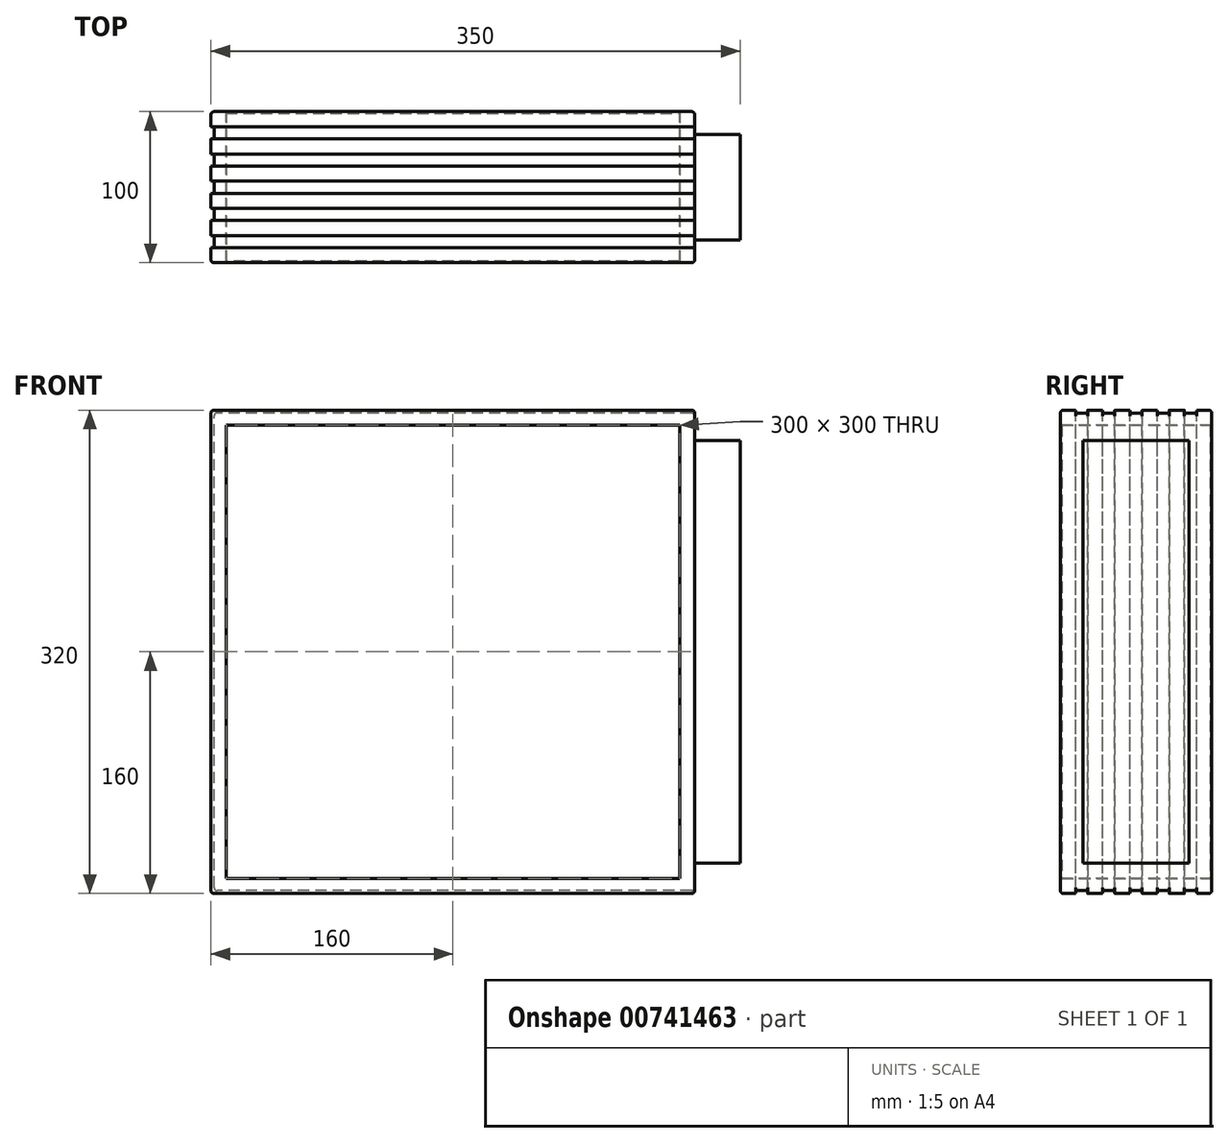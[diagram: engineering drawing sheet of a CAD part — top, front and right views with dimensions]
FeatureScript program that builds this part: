
annotation { "Feature Type Name" : "Feature", "Feature Type Description" : "" }
export const myFeature = defineFeature(function(context is Context, id is Id, definition is map)
    precondition{}
    {
        {
            var Q0;
            Q0=qCreatedBy(makeId("Front.planeOp"),FACE);
            var sketch = newSketch(context, id + "F0", { "sketchPlane" : qUnion([Q0])});
            skLineSegment(sketch, "E0.bottom", {"start": v(-1550, 0) * mm, "end": v(-1500, 0) * mm});
            skLineSegment(sketch, "E0.top", {"start": v(-1550, -2720) * mm, "end": v(-1500, -2720) * mm});
            skLineSegment(sketch, "E0.left", {"start": v(-1550, 0) * mm, "end": v(-1550, -2720) * mm});
            skLineSegment(sketch, "E0.right", {"start": v(-1500, 0) * mm, "end": v(-1500, -2720) * mm});
            skLineSegment(sketch, "E1.MirrorCS", {"start": v(1550, -2720) * mm, "end": v(1500, -2720) * mm});
            skLineSegment(sketch, "E2.MirrorCS", {"start": v(1500, 0) * mm, "end": v(1500, -2720) * mm});
            skLineSegment(sketch, "E3.MirrorCS", {"start": v(1550, 0) * mm, "end": v(1500, 0) * mm});
            skLineSegment(sketch, "E4.MirrorCS", {"start": v(1550, 0) * mm, "end": v(1550, -2720) * mm});
            skSolve(sketch);
        }
        {
            var Q0;
            Q0=qSketchRegion(id+"F0",true);
            extrude(context, id + "F1", {"entities" : qUnion([Q0]), "depth" : 100 * mm, "offsetDistance" : 25 * mm});
        }
        {
            var Q0;
            Q0=makeQuery(id+"F1.opExtrude","SWEPT_FACE",FACE,{"disambiguationData":[OSD([sQuery(id+"F0.wireOp",EDGE,"E0.bottom")])]});
            var sketch = newSketch(context, id + "F2", { "sketchPlane" : qUnion([Q0])});
            skLineSegment(sketch, "E5.bottom", {"start": v(-1550, -100) * mm, "end": v(-1870, -100) * mm});
            skLineSegment(sketch, "E5.top", {"start": v(-1550, 0) * mm, "end": v(-1870, 0) * mm});
            skLineSegment(sketch, "E5.left", {"start": v(-1550, -100) * mm, "end": v(-1550, 0) * mm});
            skLineSegment(sketch, "E5.right", {"start": v(-1870, -100) * mm, "end": v(-1870, 0) * mm});
            skLineSegment(sketch, "E6.bottom", {"start": v(-1500, -100) * mm, "end": v(1500, -100) * mm});
            skLineSegment(sketch, "E6.top", {"start": v(-1500, 0) * mm, "end": v(1500, 0) * mm});
            skLineSegment(sketch, "E6.left", {"start": v(-1500, -100) * mm, "end": v(-1500, 0) * mm});
            skLineSegment(sketch, "E6.right", {"start": v(1500, -100) * mm, "end": v(1500, 0) * mm});
            skLineSegment(sketch, "E7.bottom", {"start": v(1550, -100) * mm, "end": v(2770, -100) * mm});
            skLineSegment(sketch, "E7.top", {"start": v(1550, 0) * mm, "end": v(2770, 0) * mm});
            skLineSegment(sketch, "E7.left", {"start": v(1550, -100) * mm, "end": v(1550, 0) * mm});
            skLineSegment(sketch, "E7.right", {"start": v(2770, -100) * mm, "end": v(2770, 0) * mm});
            skSolve(sketch);
        }
        {
            var Q0;
            Q0=qSketchRegion(id+"F2",true);
            extrude(context, id + "F3", {"entities" : qUnion([Q0]), "oppositeDirection" : true, "depth" : 320 * mm, "offsetDistance" : 25 * mm});
        }
        {
            var Q0;
            Q0=makeQuery(id+"F3.opExtrude","SWEPT_FACE",FACE,{"disambiguationData":[OSD([sQuery(id+"F2.wireOp",EDGE,"E6.bottom")])]});
            var sketch = newSketch(context, id + "F4", { "sketchPlane" : qUnion([Q0])});
            skLineSegment(sketch, "E8.0", {"start": v(-1560, -10) * mm, "end": v(-1860, -10) * mm});
            skLineSegment(sketch, "E8.1", {"start": v(-1560, -310) * mm, "end": v(-1560, -10) * mm});
            skLineSegment(sketch, "E8.2", {"start": v(-1860, -310) * mm, "end": v(-1560, -310) * mm});
            skLineSegment(sketch, "E8.3", {"start": v(-1860, -10) * mm, "end": v(-1860, -310) * mm});
            skLineSegment(sketch, "E9.0", {"start": v(1490, -10) * mm, "end": v(-1490, -10) * mm});
            skLineSegment(sketch, "E9.1", {"start": v(1490, -310) * mm, "end": v(1490, -10) * mm});
            skLineSegment(sketch, "E9.2", {"start": v(-1490, -310) * mm, "end": v(1490, -310) * mm});
            skLineSegment(sketch, "E9.3", {"start": v(-1490, -10) * mm, "end": v(-1490, -310) * mm});
            skLineSegment(sketch, "E10.0", {"start": v(2760, -10) * mm, "end": v(1560, -10) * mm});
            skLineSegment(sketch, "E10.1", {"start": v(2760, -310) * mm, "end": v(2760, -10) * mm});
            skLineSegment(sketch, "E10.2", {"start": v(1560, -310) * mm, "end": v(2760, -310) * mm});
            skLineSegment(sketch, "E10.3", {"start": v(1560, -10) * mm, "end": v(1560, -310) * mm});
            skSolve(sketch);
        }
        {
            var Q0;
            Q0=qSketchRegion(id+"F4",true);
            extrude(context, id + "F5", {"entities" : qUnion([Q0]), "operationType" : NewBodyOperationType.REMOVE, "endBound" : BoundingType.THROUGH_ALL, "oppositeDirection" : true, "depth" : 25 * mm, "offsetDistance" : 25 * mm});
        }
        {
            var Q0;
            Q0=makeQuery(id+"F3.opExtrude","SWEPT_FACE",FACE,{"disambiguationData":[OSD([sQuery(id+"F2.wireOp",EDGE,"E5.right")])]});
            var sketch = newSketch(context, id + "F6", { "sketchPlane" : qUnion([Q0])});
            skLineSegment(sketch, "E11", {"start": v(10, 0) * mm, "end": v(10, -2) * mm});
            skLineSegment(sketch, "E12", {"start": v(10, -2) * mm, "end": v(18, -2) * mm});
            skLineSegment(sketch, "E13", {"start": v(18, -2) * mm, "end": v(18, 0) * mm});
            skLineSegment(sketch, "E14.1.0.0", {"start": v(36, -2) * mm, "end": v(36, 0) * mm});
            skLineSegment(sketch, "E14.1.0.1", {"start": v(28, -2) * mm, "end": v(36, -2) * mm});
            skLineSegment(sketch, "E14.1.0.2", {"start": v(28, 0) * mm, "end": v(28, -2) * mm});
            skLineSegment(sketch, "E14.2.0.0", {"start": v(54, -2) * mm, "end": v(54, 0) * mm});
            skLineSegment(sketch, "E14.2.0.1", {"start": v(46, -2) * mm, "end": v(54, -2) * mm});
            skLineSegment(sketch, "E14.2.0.2", {"start": v(46, 0) * mm, "end": v(46, -2) * mm});
            skLineSegment(sketch, "E14.3.0.0", {"start": v(72, -2) * mm, "end": v(72, 0) * mm});
            skLineSegment(sketch, "E14.3.0.1", {"start": v(64, -2) * mm, "end": v(72, -2) * mm});
            skLineSegment(sketch, "E14.3.0.2", {"start": v(64, 0) * mm, "end": v(64, -2) * mm});
            skLineSegment(sketch, "E14.4.0.0", {"start": v(90, -2) * mm, "end": v(90, 0) * mm});
            skLineSegment(sketch, "E14.4.0.1", {"start": v(82, -2) * mm, "end": v(90, -2) * mm});
            skLineSegment(sketch, "E14.4.0.2", {"start": v(82, 0) * mm, "end": v(82, -2) * mm});
            skLineSegment(sketch, "E14.direction1", {"start": v(10, -2) * mm, "end": v(28, -2) * mm, "construction": true});
            skLineSegment(sketch, "E15", {"start": v(10, 0) * mm, "end": v(18, 0) * mm});
            skLineSegment(sketch, "E16", {"start": v(28, 0) * mm, "end": v(36, 0) * mm});
            skLineSegment(sketch, "E17", {"start": v(46, 0) * mm, "end": v(54, 0) * mm});
            skLineSegment(sketch, "E18", {"start": v(64, 0) * mm, "end": v(72, 0) * mm});
            skLineSegment(sketch, "E19", {"start": v(82, 0) * mm, "end": v(90, 0) * mm});
            skLineSegment(sketch, "E20", {"start": v(100, -160) * mm, "end": v(0, -160) * mm, "construction": true});
            skLineSegment(sketch, "E21.MirrorCS", {"start": v(90, -318) * mm, "end": v(90, -320) * mm});
            skLineSegment(sketch, "E22.MirrorCS", {"start": v(64, -320) * mm, "end": v(64, -318) * mm});
            skLineSegment(sketch, "E23.MirrorCS", {"start": v(10, -320) * mm, "end": v(10, -318) * mm});
            skLineSegment(sketch, "E24.MirrorCS", {"start": v(18, -318) * mm, "end": v(18, -320) * mm});
            skLineSegment(sketch, "E25.MirrorCS", {"start": v(36, -318) * mm, "end": v(36, -320) * mm});
            skLineSegment(sketch, "E26.MirrorCS", {"start": v(28, -320) * mm, "end": v(28, -318) * mm});
            skLineSegment(sketch, "E27.MirrorCS", {"start": v(54, -318) * mm, "end": v(54, -320) * mm});
            skLineSegment(sketch, "E28.MirrorCS", {"start": v(46, -320) * mm, "end": v(46, -318) * mm});
            skLineSegment(sketch, "E29.MirrorCS", {"start": v(72, -318) * mm, "end": v(72, -320) * mm});
            skLineSegment(sketch, "E30.MirrorCS", {"start": v(82, -320) * mm, "end": v(82, -318) * mm});
            skLineSegment(sketch, "E31.MirrorCS", {"start": v(10, -320) * mm, "end": v(18, -320) * mm});
            skLineSegment(sketch, "E32.MirrorCS", {"start": v(10, -318) * mm, "end": v(18, -318) * mm});
            skLineSegment(sketch, "E33.MirrorCS", {"start": v(64, -318) * mm, "end": v(72, -318) * mm});
            skLineSegment(sketch, "E34.MirrorCS", {"start": v(64, -320) * mm, "end": v(72, -320) * mm});
            skLineSegment(sketch, "E35.MirrorCS", {"start": v(82, -320) * mm, "end": v(90, -320) * mm});
            skLineSegment(sketch, "E36.MirrorCS", {"start": v(28, -320) * mm, "end": v(36, -320) * mm});
            skLineSegment(sketch, "E37.MirrorCS", {"start": v(82, -318) * mm, "end": v(90, -318) * mm});
            skLineSegment(sketch, "E38.MirrorCS", {"start": v(10, -318) * mm, "end": v(28, -318) * mm, "construction": true});
            skLineSegment(sketch, "E39.MirrorCS", {"start": v(46, -320) * mm, "end": v(54, -320) * mm});
            skLineSegment(sketch, "E40.MirrorCS", {"start": v(28, -318) * mm, "end": v(36, -318) * mm});
            skLineSegment(sketch, "E41.MirrorCS", {"start": v(46, -318) * mm, "end": v(54, -318) * mm});
            skSolve(sketch);
        }
        {
            var Q0;
            Q0=qSketchRegion(id+"F6",true);
            extrude(context, id + "F7", {"entities" : qUnion([Q0]), "operationType" : NewBodyOperationType.REMOVE, "endBound" : BoundingType.THROUGH_ALL, "oppositeDirection" : true, "depth" : 25 * mm, "offsetDistance" : 25 * mm});
        }
        {
            var Q0;
            {var subQ0=sQuery(id+"F2.wireOp",EDGE,"E5.top");var subQ1=sQuery(id+"F2.wireOp",EDGE,"E5.left");var subQ2=sQuery(id+"F2.wireOp",EDGE,"E5.right");Q0=makeQuery(id+"F7.boolean.opBoolean","SPLIT",FACE,{"disambiguationData":[TD([makeQuery(id+"F3.opExtrude","SWEPT_FACE",FACE,{"disambiguationData":[OSD([subQ0])]})])],"derivedFrom":makeQuery(id+"F3.opExtrude","CAP_FACE",FACE,{"disambiguationData":[OSD([sQuery(id+"F2.wireOp",EDGE,"E5.bottom"),subQ0,subQ1,subQ2])],"isStart":true})});}
            var sketch = newSketch(context, id + "F8", { "sketchPlane" : qUnion([Q0])});
            skLineSegment(sketch, "E42.bottom", {"start": v(-1868, -90) * mm, "end": v(-1870, -90) * mm});
            skLineSegment(sketch, "E42.top", {"start": v(-1868, -82) * mm, "end": v(-1870, -82) * mm});
            skLineSegment(sketch, "E42.left", {"start": v(-1868, -90) * mm, "end": v(-1868, -82) * mm});
            skLineSegment(sketch, "E42.right", {"start": v(-1870, -90) * mm, "end": v(-1870, -82) * mm});
            skLineSegment(sketch, "E43.0.1.0", {"start": v(-1868, -64) * mm, "end": v(-1870, -64) * mm});
            skLineSegment(sketch, "E43.0.1.1", {"start": v(-1868, -72) * mm, "end": v(-1870, -72) * mm});
            skLineSegment(sketch, "E43.0.1.2", {"start": v(-1870, -72) * mm, "end": v(-1870, -64) * mm});
            skLineSegment(sketch, "E43.0.1.3", {"start": v(-1868, -72) * mm, "end": v(-1868, -64) * mm});
            skLineSegment(sketch, "E43.0.2.0", {"start": v(-1868, -46) * mm, "end": v(-1870, -46) * mm});
            skLineSegment(sketch, "E43.0.2.1", {"start": v(-1868, -54) * mm, "end": v(-1870, -54) * mm});
            skLineSegment(sketch, "E43.0.2.2", {"start": v(-1870, -54) * mm, "end": v(-1870, -46) * mm});
            skLineSegment(sketch, "E43.0.2.3", {"start": v(-1868, -54) * mm, "end": v(-1868, -46) * mm});
            skLineSegment(sketch, "E43.0.3.0", {"start": v(-1868, -28) * mm, "end": v(-1870, -28) * mm});
            skLineSegment(sketch, "E43.0.3.1", {"start": v(-1868, -36) * mm, "end": v(-1870, -36) * mm});
            skLineSegment(sketch, "E43.0.3.2", {"start": v(-1870, -36) * mm, "end": v(-1870, -28) * mm});
            skLineSegment(sketch, "E43.0.3.3", {"start": v(-1868, -36) * mm, "end": v(-1868, -28) * mm});
            skLineSegment(sketch, "E43.0.4.0", {"start": v(-1868, -10) * mm, "end": v(-1870, -10) * mm});
            skLineSegment(sketch, "E43.0.4.1", {"start": v(-1868, -18) * mm, "end": v(-1870, -18) * mm});
            skLineSegment(sketch, "E43.0.4.2", {"start": v(-1870, -18) * mm, "end": v(-1870, -10) * mm});
            skLineSegment(sketch, "E43.0.4.3", {"start": v(-1868, -18) * mm, "end": v(-1868, -10) * mm});
            skLineSegment(sketch, "E43.direction1", {"start": v(-2770, -90) * mm, "end": v(-1870, -90) * mm, "construction": true});
            skLineSegment(sketch, "E43.direction2", {"start": v(-1870, -90) * mm, "end": v(-1870, -72) * mm, "construction": true});
            skPoint(sketch, "E44.0", {"position": v(0, -10) * mm});
            skLineSegment(sketch, "E45.MirrorCS", {"start": v(1868, -64) * mm, "end": v(1870, -64) * mm});
            skLineSegment(sketch, "E46.MirrorCS", {"start": v(1868, -36) * mm, "end": v(1870, -36) * mm});
            skLineSegment(sketch, "E47.MirrorCS", {"start": v(1868, -90) * mm, "end": v(1870, -90) * mm});
            skLineSegment(sketch, "E48.MirrorCS", {"start": v(1868, -82) * mm, "end": v(1870, -82) * mm});
            skLineSegment(sketch, "E49.MirrorCS", {"start": v(1868, -72) * mm, "end": v(1870, -72) * mm});
            skLineSegment(sketch, "E50.MirrorCS", {"start": v(1868, -46) * mm, "end": v(1870, -46) * mm});
            skLineSegment(sketch, "E51.MirrorCS", {"start": v(1868, -54) * mm, "end": v(1870, -54) * mm});
            skLineSegment(sketch, "E52.MirrorCS", {"start": v(1870, -36) * mm, "end": v(1870, -28) * mm});
            skLineSegment(sketch, "E53.MirrorCS", {"start": v(1868, -90) * mm, "end": v(1868, -82) * mm});
            skLineSegment(sketch, "E54.MirrorCS", {"start": v(1870, -72) * mm, "end": v(1870, -64) * mm});
            skLineSegment(sketch, "E55.MirrorCS", {"start": v(1870, -54) * mm, "end": v(1870, -46) * mm});
            skLineSegment(sketch, "E56.MirrorCS", {"start": v(1868, -36) * mm, "end": v(1868, -28) * mm});
            skLineSegment(sketch, "E57.MirrorCS", {"start": v(1870, -90) * mm, "end": v(1870, -82) * mm});
            skLineSegment(sketch, "E58.MirrorCS", {"start": v(1868, -72) * mm, "end": v(1868, -64) * mm});
            skLineSegment(sketch, "E59.MirrorCS", {"start": v(1868, -54) * mm, "end": v(1868, -46) * mm});
            skLineSegment(sketch, "E60.MirrorCS", {"start": v(1868, -28) * mm, "end": v(1870, -28) * mm});
            skLineSegment(sketch, "E61.MirrorCS", {"start": v(1870, -90) * mm, "end": v(1870, -72) * mm, "construction": true});
            skLineSegment(sketch, "E62.MirrorCS", {"start": v(2770, -90) * mm, "end": v(1870, -90) * mm, "construction": true});
            skLineSegment(sketch, "E63.MirrorCS", {"start": v(1868, -18) * mm, "end": v(1870, -18) * mm});
            skLineSegment(sketch, "E64.MirrorCS", {"start": v(1870, -18) * mm, "end": v(1870, -10) * mm});
            skLineSegment(sketch, "E65.MirrorCS", {"start": v(1868, -18) * mm, "end": v(1868, -10) * mm});
            skLineSegment(sketch, "E66.MirrorCS", {"start": v(1868, -10) * mm, "end": v(1870, -10) * mm});
            skSolve(sketch);
        }
        {
            var Q0;
            Q0=qSketchRegion(id+"F8",true);
            extrude(context, id + "F9", {"entities" : qUnion([Q0]), "operationType" : NewBodyOperationType.REMOVE, "endBound" : BoundingType.THROUGH_ALL, "oppositeDirection" : true, "depth" : 25 * mm, "offsetDistance" : 25 * mm});
        }
        {
            var Q0;
            Q0=makeQuery(id+"F3.opExtrude","SWEPT_FACE",FACE,{"disambiguationData":[OSD([sQuery(id+"F2.wireOp",EDGE,"E7.top")])]});
            cPlane(context, id + "F10", {"entities" : qUnion([Q0]), "cplaneType" : CPlaneType.OFFSET, "offset" : 1 * mm, "oppositeDirection" : true, "width" : 150 * mm, "height" : 150 * mm});
        }
        {
            var Q0;
            Q0=qCreatedBy(id+"F10.planeOp",FACE);
            var sketch = newSketch(context, id + "F11", { "sketchPlane" : qUnion([Q0])});
            skLineSegment(sketch, "E67.0", {"start": v(1490, -10) * mm, "end": v(1490, -310) * mm});
            skLineSegment(sketch, "E67.1", {"start": v(-1490, -10) * mm, "end": v(1490, -10) * mm});
            skLineSegment(sketch, "E67.2", {"start": v(1490, -310) * mm, "end": v(-1490, -310) * mm});
            skLineSegment(sketch, "E67.3", {"start": v(-1490, -310) * mm, "end": v(-1490, -10) * mm});
            skLineSegment(sketch, "E67.4", {"start": v(-1560, -10) * mm, "end": v(-1560, -310) * mm});
            skLineSegment(sketch, "E67.5", {"start": v(-1560, -310) * mm, "end": v(-2760, -310) * mm});
            skLineSegment(sketch, "E67.6", {"start": v(-2760, -10) * mm, "end": v(-1560, -10) * mm});
            skLineSegment(sketch, "E67.7", {"start": v(-2760, -310) * mm, "end": v(-2760, -10) * mm});
            skLineSegment(sketch, "E67.8", {"start": v(1560, -10) * mm, "end": v(1560, -310) * mm});
            skLineSegment(sketch, "E67.9", {"start": v(1560, -310) * mm, "end": v(1860, -310) * mm});
            skLineSegment(sketch, "E67.10", {"start": v(1860, -10) * mm, "end": v(1560, -10) * mm});
            skLineSegment(sketch, "E67.11", {"start": v(1860, -310) * mm, "end": v(1860, -10) * mm});
            skSolve(sketch);
        }
        {
            var Q0;
            Q0=qSketchRegion(id+"F11",true);
            var Q1;
            Q1=makeQuery(id+"F3.opExtrude","SWEPT_FACE",FACE,{"disambiguationData":[OSD([sQuery(id+"F2.wireOp",EDGE,"E5.bottom")])]});
            extrude(context, id + "F12", {"entities" : qUnion([Q0]), "endBound" : BoundingType.UP_TO_SURFACE, "oppositeDirection" : true, "depth" : 25 * mm, "endBoundEntityFace" : qUnion([Q1]), "hasOffset" : true, "offsetDistance" : 1 * mm});
        }
        {
            var Q0;
            {var subQ0=sQuery(id+"F2.wireOp",EDGE,"E7.right");var subQ1=sQuery(id+"F2.wireOp",EDGE,"E7.top");Q0=makeQuery(id+"F7.boolean.opBoolean","SPLIT",EDGE,{"disambiguationData":[TD([makeQuery(id+"F3.opExtrude","SWEPT_FACE",FACE,{"disambiguationData":[OSD([subQ1])]})])],"derivedFrom":makeQuery(id+"F3.opExtrude","CAP_EDGE",EDGE,{"disambiguationData":[OSD([subQ0])],"isStart":true})});}
            var Q1;
            {var subQ0=sQuery(id+"F2.wireOp",EDGE,"E7.right");Q1=makeQuery(id+"F7.boolean.opBoolean","SPLIT",EDGE,{"disambiguationData":[TD([makeQuery(id+"F7.opExtrude","SWEPT_FACE",FACE,{"disambiguationData":[OSD([sQuery(id+"F6.wireOp",EDGE,"E13")])]})])],"derivedFrom":makeQuery(id+"F3.opExtrude","CAP_EDGE",EDGE,{"disambiguationData":[OSD([subQ0])],"isStart":true})});}
            var Q2;
            {var subQ0=sQuery(id+"F2.wireOp",EDGE,"E7.right");Q2=makeQuery(id+"F7.boolean.opBoolean","SPLIT",EDGE,{"disambiguationData":[TD([makeQuery(id+"F7.opExtrude","SWEPT_FACE",FACE,{"disambiguationData":[OSD([sQuery(id+"F6.wireOp",EDGE,"E14.1.0.0")])]})])],"derivedFrom":makeQuery(id+"F3.opExtrude","CAP_EDGE",EDGE,{"disambiguationData":[OSD([subQ0])],"isStart":true})});}
            var Q3;
            {var subQ0=sQuery(id+"F2.wireOp",EDGE,"E7.right");Q3=makeQuery(id+"F7.boolean.opBoolean","SPLIT",EDGE,{"disambiguationData":[TD([makeQuery(id+"F7.opExtrude","SWEPT_FACE",FACE,{"disambiguationData":[OSD([sQuery(id+"F6.wireOp",EDGE,"E14.2.0.0")])]})])],"derivedFrom":makeQuery(id+"F3.opExtrude","CAP_EDGE",EDGE,{"disambiguationData":[OSD([subQ0])],"isStart":true})});}
            var Q4;
            {var subQ0=sQuery(id+"F2.wireOp",EDGE,"E7.right");Q4=makeQuery(id+"F7.boolean.opBoolean","SPLIT",EDGE,{"disambiguationData":[TD([makeQuery(id+"F7.opExtrude","SWEPT_FACE",FACE,{"disambiguationData":[OSD([sQuery(id+"F6.wireOp",EDGE,"E14.3.0.0")])]})])],"derivedFrom":makeQuery(id+"F3.opExtrude","CAP_EDGE",EDGE,{"disambiguationData":[OSD([subQ0])],"isStart":true})});}
            var Q5;
            {var subQ0=sQuery(id+"F2.wireOp",EDGE,"E7.bottom");var subQ1=sQuery(id+"F2.wireOp",EDGE,"E7.right");Q5=makeQuery(id+"F7.boolean.opBoolean","SPLIT",EDGE,{"disambiguationData":[TD([makeQuery(id+"F3.opExtrude","SWEPT_FACE",FACE,{"disambiguationData":[OSD([subQ0])]})])],"derivedFrom":makeQuery(id+"F3.opExtrude","CAP_EDGE",EDGE,{"disambiguationData":[OSD([subQ1])],"isStart":true})});}
            var Q6;
            Q6=makeQuery(id+"F9.boolean.opBoolean","INTERSECT",EDGE,{"derivedFrom":[makeQuery(id+"F7.boolean.opBoolean","COPY",FACE,{"disambiguationData":[TD([makeQuery(id+"F3.opExtrude","SWEPT_FACE",FACE,{"disambiguationData":[OSD([sQuery(id+"F2.wireOp",EDGE,"E7.left")])]})])],"derivedFrom":makeQuery(id+"F7.opExtrude","SWEPT_FACE",FACE,{"disambiguationData":[OSD([sQuery(id+"F6.wireOp",EDGE,"E14.4.0.1")])]})}),makeQuery(id+"F9.opExtrude","SWEPT_FACE",FACE,{"disambiguationData":[OSD([sQuery(id+"F8.wireOp",EDGE,"E53.MirrorCS")])]})]});
            var Q7;
            Q7=makeQuery(id+"F9.boolean.opBoolean","INTERSECT",EDGE,{"derivedFrom":[makeQuery(id+"F7.boolean.opBoolean","COPY",FACE,{"disambiguationData":[TD([makeQuery(id+"F3.opExtrude","SWEPT_FACE",FACE,{"disambiguationData":[OSD([sQuery(id+"F2.wireOp",EDGE,"E7.left")])]})])],"derivedFrom":makeQuery(id+"F7.opExtrude","SWEPT_FACE",FACE,{"disambiguationData":[OSD([sQuery(id+"F6.wireOp",EDGE,"E14.3.0.1")])]})}),makeQuery(id+"F9.opExtrude","SWEPT_FACE",FACE,{"disambiguationData":[OSD([sQuery(id+"F8.wireOp",EDGE,"E58.MirrorCS")])]})]});
            var Q8;
            Q8=makeQuery(id+"F9.boolean.opBoolean","INTERSECT",EDGE,{"derivedFrom":[makeQuery(id+"F7.boolean.opBoolean","COPY",FACE,{"disambiguationData":[TD([makeQuery(id+"F3.opExtrude","SWEPT_FACE",FACE,{"disambiguationData":[OSD([sQuery(id+"F2.wireOp",EDGE,"E7.left")])]})])],"derivedFrom":makeQuery(id+"F7.opExtrude","SWEPT_FACE",FACE,{"disambiguationData":[OSD([sQuery(id+"F6.wireOp",EDGE,"E14.2.0.1")])]})}),makeQuery(id+"F9.opExtrude","SWEPT_FACE",FACE,{"disambiguationData":[OSD([sQuery(id+"F8.wireOp",EDGE,"E59.MirrorCS")])]})]});
            var Q9;
            Q9=makeQuery(id+"F9.boolean.opBoolean","INTERSECT",EDGE,{"derivedFrom":[makeQuery(id+"F7.boolean.opBoolean","COPY",FACE,{"disambiguationData":[TD([makeQuery(id+"F3.opExtrude","SWEPT_FACE",FACE,{"disambiguationData":[OSD([sQuery(id+"F2.wireOp",EDGE,"E7.left")])]})])],"derivedFrom":makeQuery(id+"F7.opExtrude","SWEPT_FACE",FACE,{"disambiguationData":[OSD([sQuery(id+"F6.wireOp",EDGE,"E14.1.0.1")])]})}),makeQuery(id+"F9.opExtrude","SWEPT_FACE",FACE,{"disambiguationData":[OSD([sQuery(id+"F8.wireOp",EDGE,"E56.MirrorCS")])]})]});
            var Q10;
            Q10=makeQuery(id+"F9.boolean.opBoolean","INTERSECT",EDGE,{"derivedFrom":[makeQuery(id+"F7.boolean.opBoolean","COPY",FACE,{"disambiguationData":[TD([makeQuery(id+"F3.opExtrude","SWEPT_FACE",FACE,{"disambiguationData":[OSD([sQuery(id+"F2.wireOp",EDGE,"E7.left")])]})])],"derivedFrom":makeQuery(id+"F7.opExtrude","SWEPT_FACE",FACE,{"disambiguationData":[OSD([sQuery(id+"F6.wireOp",EDGE,"E12")])]})}),makeQuery(id+"F9.opExtrude","SWEPT_FACE",FACE,{"disambiguationData":[OSD([sQuery(id+"F8.wireOp",EDGE,"E65.MirrorCS")])]})]});
            var Q11;
            {var subQ0=sQuery(id+"F2.wireOp",EDGE,"E7.left");var subQ1=sQuery(id+"F2.wireOp",EDGE,"E7.top");Q11=makeQuery(id+"F7.boolean.opBoolean","SPLIT",EDGE,{"disambiguationData":[TD([makeQuery(id+"F3.opExtrude","SWEPT_FACE",FACE,{"disambiguationData":[OSD([subQ1])]})])],"derivedFrom":makeQuery(id+"F3.opExtrude","CAP_EDGE",EDGE,{"disambiguationData":[OSD([subQ0])],"isStart":true})});}
            var Q12;
            {var subQ0=sQuery(id+"F2.wireOp",EDGE,"E7.left");Q12=makeQuery(id+"F7.boolean.opBoolean","SPLIT",EDGE,{"disambiguationData":[TD([makeQuery(id+"F7.opExtrude","SWEPT_FACE",FACE,{"disambiguationData":[OSD([sQuery(id+"F6.wireOp",EDGE,"E13")])]})])],"derivedFrom":makeQuery(id+"F3.opExtrude","CAP_EDGE",EDGE,{"disambiguationData":[OSD([subQ0])],"isStart":true})});}
            var Q13;
            {var subQ0=sQuery(id+"F2.wireOp",EDGE,"E7.left");Q13=makeQuery(id+"F7.boolean.opBoolean","SPLIT",EDGE,{"disambiguationData":[TD([makeQuery(id+"F7.opExtrude","SWEPT_FACE",FACE,{"disambiguationData":[OSD([sQuery(id+"F6.wireOp",EDGE,"E14.1.0.0")])]})])],"derivedFrom":makeQuery(id+"F3.opExtrude","CAP_EDGE",EDGE,{"disambiguationData":[OSD([subQ0])],"isStart":true})});}
            var Q14;
            {var subQ0=sQuery(id+"F2.wireOp",EDGE,"E7.left");Q14=makeQuery(id+"F7.boolean.opBoolean","SPLIT",EDGE,{"disambiguationData":[TD([makeQuery(id+"F7.opExtrude","SWEPT_FACE",FACE,{"disambiguationData":[OSD([sQuery(id+"F6.wireOp",EDGE,"E14.2.0.0")])]})])],"derivedFrom":makeQuery(id+"F3.opExtrude","CAP_EDGE",EDGE,{"disambiguationData":[OSD([subQ0])],"isStart":true})});}
            var Q15;
            {var subQ0=sQuery(id+"F2.wireOp",EDGE,"E7.bottom");var subQ1=sQuery(id+"F2.wireOp",EDGE,"E7.left");Q15=makeQuery(id+"F7.boolean.opBoolean","SPLIT",EDGE,{"disambiguationData":[TD([makeQuery(id+"F3.opExtrude","SWEPT_FACE",FACE,{"disambiguationData":[OSD([subQ0])]})])],"derivedFrom":makeQuery(id+"F3.opExtrude","CAP_EDGE",EDGE,{"disambiguationData":[OSD([subQ1])],"isStart":true})});}
            var Q16;
            Q16=makeQuery(id+"F1.opExtrude","SWEPT_EDGE",EDGE,{"disambiguationData":[OSD([sQuery(id+"F0.wireOp",EDGE,"E3.MirrorCS"),sQuery(id+"F0.wireOp",EDGE,"E4.MirrorCS")])]});
            var Q17;
            {var subQ0=sQuery(id+"F2.wireOp",EDGE,"E7.left");Q17=makeQuery(id+"F7.boolean.opBoolean","SPLIT",EDGE,{"disambiguationData":[TD([makeQuery(id+"F7.opExtrude","SWEPT_FACE",FACE,{"disambiguationData":[OSD([sQuery(id+"F6.wireOp",EDGE,"E14.3.0.0")])]})])],"derivedFrom":makeQuery(id+"F3.opExtrude","CAP_EDGE",EDGE,{"disambiguationData":[OSD([subQ0])],"isStart":true})});}
            var Q18;
            Q18=makeQuery(id+"F7.boolean.opBoolean","INTERSECT",EDGE,{"derivedFrom":[makeQuery(id+"F3.opExtrude","SWEPT_FACE",FACE,{"disambiguationData":[OSD([sQuery(id+"F2.wireOp",EDGE,"E7.left")])]}),makeQuery(id+"F7.opExtrude","SWEPT_FACE",FACE,{"disambiguationData":[OSD([sQuery(id+"F6.wireOp",EDGE,"E14.4.0.1")])]})]});
            var Q19;
            Q19=makeQuery(id+"F7.boolean.opBoolean","INTERSECT",EDGE,{"derivedFrom":[makeQuery(id+"F3.opExtrude","SWEPT_FACE",FACE,{"disambiguationData":[OSD([sQuery(id+"F2.wireOp",EDGE,"E7.left")])]}),makeQuery(id+"F7.opExtrude","SWEPT_FACE",FACE,{"disambiguationData":[OSD([sQuery(id+"F6.wireOp",EDGE,"E14.3.0.1")])]})]});
            var Q20;
            Q20=makeQuery(id+"F7.boolean.opBoolean","INTERSECT",EDGE,{"derivedFrom":[makeQuery(id+"F3.opExtrude","SWEPT_FACE",FACE,{"disambiguationData":[OSD([sQuery(id+"F2.wireOp",EDGE,"E7.left")])]}),makeQuery(id+"F7.opExtrude","SWEPT_FACE",FACE,{"disambiguationData":[OSD([sQuery(id+"F6.wireOp",EDGE,"E14.2.0.1")])]})]});
            var Q21;
            Q21=makeQuery(id+"F7.boolean.opBoolean","INTERSECT",EDGE,{"derivedFrom":[makeQuery(id+"F3.opExtrude","SWEPT_FACE",FACE,{"disambiguationData":[OSD([sQuery(id+"F2.wireOp",EDGE,"E7.left")])]}),makeQuery(id+"F7.opExtrude","SWEPT_FACE",FACE,{"disambiguationData":[OSD([sQuery(id+"F6.wireOp",EDGE,"E14.1.0.1")])]})]});
            var Q22;
            Q22=makeQuery(id+"F7.boolean.opBoolean","INTERSECT",EDGE,{"derivedFrom":[makeQuery(id+"F3.opExtrude","SWEPT_FACE",FACE,{"disambiguationData":[OSD([sQuery(id+"F2.wireOp",EDGE,"E7.left")])]}),makeQuery(id+"F7.opExtrude","SWEPT_FACE",FACE,{"disambiguationData":[OSD([sQuery(id+"F6.wireOp",EDGE,"E12")])]})]});
            var Q23;
            Q23=makeQuery(id+"F1.opExtrude","SWEPT_FACE",FACE,{"disambiguationData":[OSD([sQuery(id+"F0.wireOp",EDGE,"E3.MirrorCS")])]});
            var Q24;
            {var subQ0=sQuery(id+"F2.wireOp",EDGE,"E6.right");Q24=makeQuery(id+"F7.boolean.opBoolean","SPLIT",EDGE,{"disambiguationData":[TD([makeQuery(id+"F7.opExtrude","SWEPT_FACE",FACE,{"disambiguationData":[OSD([sQuery(id+"F6.wireOp",EDGE,"E14.1.0.0")])]})])],"derivedFrom":makeQuery(id+"F3.opExtrude","CAP_EDGE",EDGE,{"disambiguationData":[OSD([subQ0])],"isStart":true})});}
            var Q25;
            {var subQ0=sQuery(id+"F2.wireOp",EDGE,"E6.right");Q25=makeQuery(id+"F7.boolean.opBoolean","SPLIT",EDGE,{"disambiguationData":[TD([makeQuery(id+"F7.opExtrude","SWEPT_FACE",FACE,{"disambiguationData":[OSD([sQuery(id+"F6.wireOp",EDGE,"E13")])]})])],"derivedFrom":makeQuery(id+"F3.opExtrude","CAP_EDGE",EDGE,{"disambiguationData":[OSD([subQ0])],"isStart":true})});}
            var Q26;
            {var subQ0=sQuery(id+"F2.wireOp",EDGE,"E6.right");var subQ1=sQuery(id+"F2.wireOp",EDGE,"E6.top");Q26=makeQuery(id+"F7.boolean.opBoolean","SPLIT",EDGE,{"disambiguationData":[TD([makeQuery(id+"F3.opExtrude","SWEPT_FACE",FACE,{"disambiguationData":[OSD([subQ1])]})])],"derivedFrom":makeQuery(id+"F3.opExtrude","CAP_EDGE",EDGE,{"disambiguationData":[OSD([subQ0])],"isStart":true})});}
            var Q27;
            {var subQ0=sQuery(id+"F2.wireOp",EDGE,"E6.right");Q27=makeQuery(id+"F7.boolean.opBoolean","SPLIT",EDGE,{"disambiguationData":[TD([makeQuery(id+"F7.opExtrude","SWEPT_FACE",FACE,{"disambiguationData":[OSD([sQuery(id+"F6.wireOp",EDGE,"E14.2.0.0")])]})])],"derivedFrom":makeQuery(id+"F3.opExtrude","CAP_EDGE",EDGE,{"disambiguationData":[OSD([subQ0])],"isStart":true})});}
            var Q28;
            {var subQ0=sQuery(id+"F2.wireOp",EDGE,"E6.right");Q28=makeQuery(id+"F7.boolean.opBoolean","SPLIT",EDGE,{"disambiguationData":[TD([makeQuery(id+"F7.opExtrude","SWEPT_FACE",FACE,{"disambiguationData":[OSD([sQuery(id+"F6.wireOp",EDGE,"E14.3.0.0")])]})])],"derivedFrom":makeQuery(id+"F3.opExtrude","CAP_EDGE",EDGE,{"disambiguationData":[OSD([subQ0])],"isStart":true})});}
            var Q29;
            {var subQ0=sQuery(id+"F2.wireOp",EDGE,"E6.bottom");var subQ1=sQuery(id+"F2.wireOp",EDGE,"E6.right");Q29=makeQuery(id+"F7.boolean.opBoolean","SPLIT",EDGE,{"disambiguationData":[TD([makeQuery(id+"F3.opExtrude","SWEPT_FACE",FACE,{"disambiguationData":[OSD([subQ0])]})])],"derivedFrom":makeQuery(id+"F3.opExtrude","CAP_EDGE",EDGE,{"disambiguationData":[OSD([subQ1])],"isStart":true})});}
            var Q30;
            Q30=makeQuery(id+"F7.boolean.opBoolean","INTERSECT",EDGE,{"derivedFrom":[makeQuery(id+"F3.opExtrude","SWEPT_FACE",FACE,{"disambiguationData":[OSD([sQuery(id+"F2.wireOp",EDGE,"E6.right")])]}),makeQuery(id+"F7.opExtrude","SWEPT_FACE",FACE,{"disambiguationData":[OSD([sQuery(id+"F6.wireOp",EDGE,"E14.4.0.1")])]})]});
            var Q31;
            Q31=makeQuery(id+"F7.boolean.opBoolean","INTERSECT",EDGE,{"derivedFrom":[makeQuery(id+"F3.opExtrude","SWEPT_FACE",FACE,{"disambiguationData":[OSD([sQuery(id+"F2.wireOp",EDGE,"E6.right")])]}),makeQuery(id+"F7.opExtrude","SWEPT_FACE",FACE,{"disambiguationData":[OSD([sQuery(id+"F6.wireOp",EDGE,"E14.3.0.1")])]})]});
            var Q32;
            Q32=makeQuery(id+"F7.boolean.opBoolean","INTERSECT",EDGE,{"derivedFrom":[makeQuery(id+"F3.opExtrude","SWEPT_FACE",FACE,{"disambiguationData":[OSD([sQuery(id+"F2.wireOp",EDGE,"E6.right")])]}),makeQuery(id+"F7.opExtrude","SWEPT_FACE",FACE,{"disambiguationData":[OSD([sQuery(id+"F6.wireOp",EDGE,"E14.2.0.1")])]})]});
            var Q33;
            Q33=makeQuery(id+"F7.boolean.opBoolean","INTERSECT",EDGE,{"derivedFrom":[makeQuery(id+"F3.opExtrude","SWEPT_FACE",FACE,{"disambiguationData":[OSD([sQuery(id+"F2.wireOp",EDGE,"E6.right")])]}),makeQuery(id+"F7.opExtrude","SWEPT_FACE",FACE,{"disambiguationData":[OSD([sQuery(id+"F6.wireOp",EDGE,"E14.1.0.1")])]})]});
            var Q34;
            Q34=makeQuery(id+"F7.boolean.opBoolean","INTERSECT",EDGE,{"derivedFrom":[makeQuery(id+"F3.opExtrude","SWEPT_FACE",FACE,{"disambiguationData":[OSD([sQuery(id+"F2.wireOp",EDGE,"E6.right")])]}),makeQuery(id+"F7.opExtrude","SWEPT_FACE",FACE,{"disambiguationData":[OSD([sQuery(id+"F6.wireOp",EDGE,"E12")])]})]});
            var Q35;
            {var subQ0=sQuery(id+"F2.wireOp",EDGE,"E7.right");var subQ1=sQuery(id+"F2.wireOp",EDGE,"E7.top");Q35=makeQuery(id+"F7.boolean.opBoolean","SPLIT",EDGE,{"disambiguationData":[TD([makeQuery(id+"F3.opExtrude","SWEPT_FACE",FACE,{"disambiguationData":[OSD([subQ1])]})])],"derivedFrom":makeQuery(id+"F3.opExtrude","CAP_EDGE",EDGE,{"disambiguationData":[OSD([subQ0])],"isStart":false})});}
            var Q36;
            Q36=makeQuery(id+"F9.boolean.opBoolean","INTERSECT",EDGE,{"derivedFrom":[makeQuery(id+"F7.boolean.opBoolean","COPY",FACE,{"disambiguationData":[TD([makeQuery(id+"F3.opExtrude","SWEPT_FACE",FACE,{"disambiguationData":[OSD([sQuery(id+"F2.wireOp",EDGE,"E7.left")])]})])],"derivedFrom":makeQuery(id+"F7.opExtrude","SWEPT_FACE",FACE,{"disambiguationData":[OSD([sQuery(id+"F6.wireOp",EDGE,"E32.MirrorCS")])]})}),makeQuery(id+"F9.opExtrude","SWEPT_FACE",FACE,{"disambiguationData":[OSD([sQuery(id+"F8.wireOp",EDGE,"E65.MirrorCS")])]})]});
            var Q37;
            {var subQ0=sQuery(id+"F2.wireOp",EDGE,"E7.right");Q37=makeQuery(id+"F7.boolean.opBoolean","SPLIT",EDGE,{"disambiguationData":[TD([makeQuery(id+"F7.opExtrude","SWEPT_FACE",FACE,{"disambiguationData":[OSD([sQuery(id+"F6.wireOp",EDGE,"E24.MirrorCS")])]})])],"derivedFrom":makeQuery(id+"F3.opExtrude","CAP_EDGE",EDGE,{"disambiguationData":[OSD([subQ0])],"isStart":false})});}
            var Q38;
            Q38=makeQuery(id+"F9.boolean.opBoolean","INTERSECT",EDGE,{"derivedFrom":[makeQuery(id+"F7.boolean.opBoolean","COPY",FACE,{"disambiguationData":[TD([makeQuery(id+"F3.opExtrude","SWEPT_FACE",FACE,{"disambiguationData":[OSD([sQuery(id+"F2.wireOp",EDGE,"E7.left")])]})])],"derivedFrom":makeQuery(id+"F7.opExtrude","SWEPT_FACE",FACE,{"disambiguationData":[OSD([sQuery(id+"F6.wireOp",EDGE,"E40.MirrorCS")])]})}),makeQuery(id+"F9.opExtrude","SWEPT_FACE",FACE,{"disambiguationData":[OSD([sQuery(id+"F8.wireOp",EDGE,"E56.MirrorCS")])]})]});
            var Q39;
            {var subQ0=sQuery(id+"F2.wireOp",EDGE,"E7.right");Q39=makeQuery(id+"F7.boolean.opBoolean","SPLIT",EDGE,{"disambiguationData":[TD([makeQuery(id+"F7.opExtrude","SWEPT_FACE",FACE,{"disambiguationData":[OSD([sQuery(id+"F6.wireOp",EDGE,"E25.MirrorCS")])]})])],"derivedFrom":makeQuery(id+"F3.opExtrude","CAP_EDGE",EDGE,{"disambiguationData":[OSD([subQ0])],"isStart":false})});}
            var Q40;
            Q40=makeQuery(id+"F9.boolean.opBoolean","INTERSECT",EDGE,{"derivedFrom":[makeQuery(id+"F7.boolean.opBoolean","COPY",FACE,{"disambiguationData":[TD([makeQuery(id+"F3.opExtrude","SWEPT_FACE",FACE,{"disambiguationData":[OSD([sQuery(id+"F2.wireOp",EDGE,"E7.left")])]})])],"derivedFrom":makeQuery(id+"F7.opExtrude","SWEPT_FACE",FACE,{"disambiguationData":[OSD([sQuery(id+"F6.wireOp",EDGE,"E41.MirrorCS")])]})}),makeQuery(id+"F9.opExtrude","SWEPT_FACE",FACE,{"disambiguationData":[OSD([sQuery(id+"F8.wireOp",EDGE,"E59.MirrorCS")])]})]});
            var Q41;
            {var subQ0=sQuery(id+"F2.wireOp",EDGE,"E7.right");Q41=makeQuery(id+"F7.boolean.opBoolean","SPLIT",EDGE,{"disambiguationData":[TD([makeQuery(id+"F7.opExtrude","SWEPT_FACE",FACE,{"disambiguationData":[OSD([sQuery(id+"F6.wireOp",EDGE,"E22.MirrorCS")])]})])],"derivedFrom":makeQuery(id+"F3.opExtrude","CAP_EDGE",EDGE,{"disambiguationData":[OSD([subQ0])],"isStart":false})});}
            var Q42;
            Q42=makeQuery(id+"F9.boolean.opBoolean","INTERSECT",EDGE,{"derivedFrom":[makeQuery(id+"F7.boolean.opBoolean","COPY",FACE,{"disambiguationData":[TD([makeQuery(id+"F3.opExtrude","SWEPT_FACE",FACE,{"disambiguationData":[OSD([sQuery(id+"F2.wireOp",EDGE,"E7.left")])]})])],"derivedFrom":makeQuery(id+"F7.opExtrude","SWEPT_FACE",FACE,{"disambiguationData":[OSD([sQuery(id+"F6.wireOp",EDGE,"E33.MirrorCS")])]})}),makeQuery(id+"F9.opExtrude","SWEPT_FACE",FACE,{"disambiguationData":[OSD([sQuery(id+"F8.wireOp",EDGE,"E58.MirrorCS")])]})]});
            var Q43;
            {var subQ0=sQuery(id+"F2.wireOp",EDGE,"E7.right");Q43=makeQuery(id+"F7.boolean.opBoolean","SPLIT",EDGE,{"disambiguationData":[TD([makeQuery(id+"F7.opExtrude","SWEPT_FACE",FACE,{"disambiguationData":[OSD([sQuery(id+"F6.wireOp",EDGE,"E29.MirrorCS")])]})])],"derivedFrom":makeQuery(id+"F3.opExtrude","CAP_EDGE",EDGE,{"disambiguationData":[OSD([subQ0])],"isStart":false})});}
            var Q44;
            Q44=makeQuery(id+"F9.boolean.opBoolean","INTERSECT",EDGE,{"derivedFrom":[makeQuery(id+"F7.boolean.opBoolean","COPY",FACE,{"disambiguationData":[TD([makeQuery(id+"F3.opExtrude","SWEPT_FACE",FACE,{"disambiguationData":[OSD([sQuery(id+"F2.wireOp",EDGE,"E7.left")])]})])],"derivedFrom":makeQuery(id+"F7.opExtrude","SWEPT_FACE",FACE,{"disambiguationData":[OSD([sQuery(id+"F6.wireOp",EDGE,"E37.MirrorCS")])]})}),makeQuery(id+"F9.opExtrude","SWEPT_FACE",FACE,{"disambiguationData":[OSD([sQuery(id+"F8.wireOp",EDGE,"E53.MirrorCS")])]})]});
            var Q45;
            {var subQ0=sQuery(id+"F2.wireOp",EDGE,"E7.bottom");var subQ1=sQuery(id+"F2.wireOp",EDGE,"E7.right");Q45=makeQuery(id+"F7.boolean.opBoolean","SPLIT",EDGE,{"disambiguationData":[TD([makeQuery(id+"F3.opExtrude","SWEPT_FACE",FACE,{"disambiguationData":[OSD([subQ0])]})])],"derivedFrom":makeQuery(id+"F3.opExtrude","CAP_EDGE",EDGE,{"disambiguationData":[OSD([subQ1])],"isStart":false})});}
            var Q46;
            {var subQ0=sQuery(id+"F2.wireOp",EDGE,"E7.left");var subQ1=sQuery(id+"F2.wireOp",EDGE,"E7.top");Q46=makeQuery(id+"F7.boolean.opBoolean","SPLIT",EDGE,{"disambiguationData":[TD([makeQuery(id+"F3.opExtrude","SWEPT_FACE",FACE,{"disambiguationData":[OSD([subQ1])]})])],"derivedFrom":makeQuery(id+"F3.opExtrude","CAP_EDGE",EDGE,{"disambiguationData":[OSD([subQ0])],"isStart":false})});}
            var Q47;
            Q47=makeQuery(id+"F7.boolean.opBoolean","INTERSECT",EDGE,{"derivedFrom":[makeQuery(id+"F3.opExtrude","SWEPT_FACE",FACE,{"disambiguationData":[OSD([sQuery(id+"F2.wireOp",EDGE,"E7.left")])]}),makeQuery(id+"F7.opExtrude","SWEPT_FACE",FACE,{"disambiguationData":[OSD([sQuery(id+"F6.wireOp",EDGE,"E32.MirrorCS")])]})]});
            var Q48;
            {var subQ0=sQuery(id+"F2.wireOp",EDGE,"E7.left");Q48=makeQuery(id+"F7.boolean.opBoolean","SPLIT",EDGE,{"disambiguationData":[TD([makeQuery(id+"F7.opExtrude","SWEPT_FACE",FACE,{"disambiguationData":[OSD([sQuery(id+"F6.wireOp",EDGE,"E24.MirrorCS")])]})])],"derivedFrom":makeQuery(id+"F3.opExtrude","CAP_EDGE",EDGE,{"disambiguationData":[OSD([subQ0])],"isStart":false})});}
            var Q49;
            Q49=makeQuery(id+"F7.boolean.opBoolean","INTERSECT",EDGE,{"derivedFrom":[makeQuery(id+"F3.opExtrude","SWEPT_FACE",FACE,{"disambiguationData":[OSD([sQuery(id+"F2.wireOp",EDGE,"E7.left")])]}),makeQuery(id+"F7.opExtrude","SWEPT_FACE",FACE,{"disambiguationData":[OSD([sQuery(id+"F6.wireOp",EDGE,"E40.MirrorCS")])]})]});
            var Q50;
            {var subQ0=sQuery(id+"F2.wireOp",EDGE,"E7.left");Q50=makeQuery(id+"F7.boolean.opBoolean","SPLIT",EDGE,{"disambiguationData":[TD([makeQuery(id+"F7.opExtrude","SWEPT_FACE",FACE,{"disambiguationData":[OSD([sQuery(id+"F6.wireOp",EDGE,"E25.MirrorCS")])]})])],"derivedFrom":makeQuery(id+"F3.opExtrude","CAP_EDGE",EDGE,{"disambiguationData":[OSD([subQ0])],"isStart":false})});}
            var Q51;
            Q51=makeQuery(id+"F7.boolean.opBoolean","INTERSECT",EDGE,{"derivedFrom":[makeQuery(id+"F3.opExtrude","SWEPT_FACE",FACE,{"disambiguationData":[OSD([sQuery(id+"F2.wireOp",EDGE,"E7.left")])]}),makeQuery(id+"F7.opExtrude","SWEPT_FACE",FACE,{"disambiguationData":[OSD([sQuery(id+"F6.wireOp",EDGE,"E41.MirrorCS")])]})]});
            var Q52;
            {var subQ0=sQuery(id+"F2.wireOp",EDGE,"E7.left");Q52=makeQuery(id+"F7.boolean.opBoolean","SPLIT",EDGE,{"disambiguationData":[TD([makeQuery(id+"F7.opExtrude","SWEPT_FACE",FACE,{"disambiguationData":[OSD([sQuery(id+"F6.wireOp",EDGE,"E22.MirrorCS")])]})])],"derivedFrom":makeQuery(id+"F3.opExtrude","CAP_EDGE",EDGE,{"disambiguationData":[OSD([subQ0])],"isStart":false})});}
            var Q53;
            Q53=makeQuery(id+"F7.boolean.opBoolean","INTERSECT",EDGE,{"derivedFrom":[makeQuery(id+"F3.opExtrude","SWEPT_FACE",FACE,{"disambiguationData":[OSD([sQuery(id+"F2.wireOp",EDGE,"E7.left")])]}),makeQuery(id+"F7.opExtrude","SWEPT_FACE",FACE,{"disambiguationData":[OSD([sQuery(id+"F6.wireOp",EDGE,"E33.MirrorCS")])]})]});
            var Q54;
            {var subQ0=sQuery(id+"F2.wireOp",EDGE,"E7.left");Q54=makeQuery(id+"F7.boolean.opBoolean","SPLIT",EDGE,{"disambiguationData":[TD([makeQuery(id+"F7.opExtrude","SWEPT_FACE",FACE,{"disambiguationData":[OSD([sQuery(id+"F6.wireOp",EDGE,"E29.MirrorCS")])]})])],"derivedFrom":makeQuery(id+"F3.opExtrude","CAP_EDGE",EDGE,{"disambiguationData":[OSD([subQ0])],"isStart":false})});}
            var Q55;
            Q55=makeQuery(id+"F7.boolean.opBoolean","INTERSECT",EDGE,{"derivedFrom":[makeQuery(id+"F3.opExtrude","SWEPT_FACE",FACE,{"disambiguationData":[OSD([sQuery(id+"F2.wireOp",EDGE,"E7.left")])]}),makeQuery(id+"F7.opExtrude","SWEPT_FACE",FACE,{"disambiguationData":[OSD([sQuery(id+"F6.wireOp",EDGE,"E37.MirrorCS")])]})]});
            var Q56;
            {var subQ0=sQuery(id+"F2.wireOp",EDGE,"E7.bottom");var subQ1=sQuery(id+"F2.wireOp",EDGE,"E7.left");Q56=makeQuery(id+"F7.boolean.opBoolean","SPLIT",EDGE,{"disambiguationData":[TD([makeQuery(id+"F3.opExtrude","SWEPT_FACE",FACE,{"disambiguationData":[OSD([subQ0])]})])],"derivedFrom":makeQuery(id+"F3.opExtrude","CAP_EDGE",EDGE,{"disambiguationData":[OSD([subQ1])],"isStart":false})});}
            var Q57;
            {var subQ0=sQuery(id+"F2.wireOp",EDGE,"E6.bottom");var subQ1=sQuery(id+"F2.wireOp",EDGE,"E6.right");Q57=makeQuery(id+"F7.boolean.opBoolean","SPLIT",EDGE,{"disambiguationData":[TD([makeQuery(id+"F3.opExtrude","SWEPT_FACE",FACE,{"disambiguationData":[OSD([subQ0])]})])],"derivedFrom":makeQuery(id+"F3.opExtrude","CAP_EDGE",EDGE,{"disambiguationData":[OSD([subQ1])],"isStart":false})});}
            var Q58;
            Q58=makeQuery(id+"F7.boolean.opBoolean","INTERSECT",EDGE,{"derivedFrom":[makeQuery(id+"F3.opExtrude","SWEPT_FACE",FACE,{"disambiguationData":[OSD([sQuery(id+"F2.wireOp",EDGE,"E6.right")])]}),makeQuery(id+"F7.opExtrude","SWEPT_FACE",FACE,{"disambiguationData":[OSD([sQuery(id+"F6.wireOp",EDGE,"E37.MirrorCS")])]})]});
            var Q59;
            {var subQ0=sQuery(id+"F2.wireOp",EDGE,"E6.right");Q59=makeQuery(id+"F7.boolean.opBoolean","SPLIT",EDGE,{"disambiguationData":[TD([makeQuery(id+"F7.opExtrude","SWEPT_FACE",FACE,{"disambiguationData":[OSD([sQuery(id+"F6.wireOp",EDGE,"E29.MirrorCS")])]})])],"derivedFrom":makeQuery(id+"F3.opExtrude","CAP_EDGE",EDGE,{"disambiguationData":[OSD([subQ0])],"isStart":false})});}
            var Q60;
            Q60=makeQuery(id+"F7.boolean.opBoolean","INTERSECT",EDGE,{"derivedFrom":[makeQuery(id+"F3.opExtrude","SWEPT_FACE",FACE,{"disambiguationData":[OSD([sQuery(id+"F2.wireOp",EDGE,"E6.right")])]}),makeQuery(id+"F7.opExtrude","SWEPT_FACE",FACE,{"disambiguationData":[OSD([sQuery(id+"F6.wireOp",EDGE,"E33.MirrorCS")])]})]});
            var Q61;
            {var subQ0=sQuery(id+"F2.wireOp",EDGE,"E6.right");Q61=makeQuery(id+"F7.boolean.opBoolean","SPLIT",EDGE,{"disambiguationData":[TD([makeQuery(id+"F7.opExtrude","SWEPT_FACE",FACE,{"disambiguationData":[OSD([sQuery(id+"F6.wireOp",EDGE,"E22.MirrorCS")])]})])],"derivedFrom":makeQuery(id+"F3.opExtrude","CAP_EDGE",EDGE,{"disambiguationData":[OSD([subQ0])],"isStart":false})});}
            var Q62;
            Q62=makeQuery(id+"F7.boolean.opBoolean","INTERSECT",EDGE,{"derivedFrom":[makeQuery(id+"F3.opExtrude","SWEPT_FACE",FACE,{"disambiguationData":[OSD([sQuery(id+"F2.wireOp",EDGE,"E6.right")])]}),makeQuery(id+"F7.opExtrude","SWEPT_FACE",FACE,{"disambiguationData":[OSD([sQuery(id+"F6.wireOp",EDGE,"E41.MirrorCS")])]})]});
            var Q63;
            {var subQ0=sQuery(id+"F2.wireOp",EDGE,"E6.right");Q63=makeQuery(id+"F7.boolean.opBoolean","SPLIT",EDGE,{"disambiguationData":[TD([makeQuery(id+"F7.opExtrude","SWEPT_FACE",FACE,{"disambiguationData":[OSD([sQuery(id+"F6.wireOp",EDGE,"E25.MirrorCS")])]})])],"derivedFrom":makeQuery(id+"F3.opExtrude","CAP_EDGE",EDGE,{"disambiguationData":[OSD([subQ0])],"isStart":false})});}
            var Q64;
            Q64=makeQuery(id+"F7.boolean.opBoolean","INTERSECT",EDGE,{"derivedFrom":[makeQuery(id+"F3.opExtrude","SWEPT_FACE",FACE,{"disambiguationData":[OSD([sQuery(id+"F2.wireOp",EDGE,"E6.right")])]}),makeQuery(id+"F7.opExtrude","SWEPT_FACE",FACE,{"disambiguationData":[OSD([sQuery(id+"F6.wireOp",EDGE,"E40.MirrorCS")])]})]});
            var Q65;
            {var subQ0=sQuery(id+"F2.wireOp",EDGE,"E6.right");Q65=makeQuery(id+"F7.boolean.opBoolean","SPLIT",EDGE,{"disambiguationData":[TD([makeQuery(id+"F7.opExtrude","SWEPT_FACE",FACE,{"disambiguationData":[OSD([sQuery(id+"F6.wireOp",EDGE,"E24.MirrorCS")])]})])],"derivedFrom":makeQuery(id+"F3.opExtrude","CAP_EDGE",EDGE,{"disambiguationData":[OSD([subQ0])],"isStart":false})});}
            var Q66;
            Q66=makeQuery(id+"F7.boolean.opBoolean","INTERSECT",EDGE,{"derivedFrom":[makeQuery(id+"F3.opExtrude","SWEPT_FACE",FACE,{"disambiguationData":[OSD([sQuery(id+"F2.wireOp",EDGE,"E6.right")])]}),makeQuery(id+"F7.opExtrude","SWEPT_FACE",FACE,{"disambiguationData":[OSD([sQuery(id+"F6.wireOp",EDGE,"E32.MirrorCS")])]})]});
            var Q67;
            {var subQ0=sQuery(id+"F2.wireOp",EDGE,"E6.right");var subQ1=sQuery(id+"F2.wireOp",EDGE,"E6.top");Q67=makeQuery(id+"F7.boolean.opBoolean","SPLIT",EDGE,{"disambiguationData":[TD([makeQuery(id+"F3.opExtrude","SWEPT_FACE",FACE,{"disambiguationData":[OSD([subQ1])]})])],"derivedFrom":makeQuery(id+"F3.opExtrude","CAP_EDGE",EDGE,{"disambiguationData":[OSD([subQ0])],"isStart":false})});}
            var Q68;
            {var subQ0=sQuery(id+"F2.wireOp",EDGE,"E6.left");var subQ1=sQuery(id+"F2.wireOp",EDGE,"E6.top");Q68=makeQuery(id+"F7.boolean.opBoolean","SPLIT",EDGE,{"disambiguationData":[TD([makeQuery(id+"F3.opExtrude","SWEPT_FACE",FACE,{"disambiguationData":[OSD([subQ1])]})])],"derivedFrom":makeQuery(id+"F3.opExtrude","CAP_EDGE",EDGE,{"disambiguationData":[OSD([subQ0])],"isStart":false})});}
            var Q69;
            {var subQ0=sQuery(id+"F2.wireOp",EDGE,"E6.left");Q69=makeQuery(id+"F7.boolean.opBoolean","SPLIT",EDGE,{"disambiguationData":[TD([makeQuery(id+"F7.opExtrude","SWEPT_FACE",FACE,{"disambiguationData":[OSD([sQuery(id+"F6.wireOp",EDGE,"E24.MirrorCS")])]})])],"derivedFrom":makeQuery(id+"F3.opExtrude","CAP_EDGE",EDGE,{"disambiguationData":[OSD([subQ0])],"isStart":false})});}
            var Q70;
            Q70=makeQuery(id+"F7.boolean.opBoolean","INTERSECT",EDGE,{"derivedFrom":[makeQuery(id+"F3.opExtrude","SWEPT_FACE",FACE,{"disambiguationData":[OSD([sQuery(id+"F2.wireOp",EDGE,"E6.left")])]}),makeQuery(id+"F7.opExtrude","SWEPT_FACE",FACE,{"disambiguationData":[OSD([sQuery(id+"F6.wireOp",EDGE,"E40.MirrorCS")])]})]});
            var Q71;
            {var subQ0=sQuery(id+"F2.wireOp",EDGE,"E6.left");Q71=makeQuery(id+"F7.boolean.opBoolean","SPLIT",EDGE,{"disambiguationData":[TD([makeQuery(id+"F7.opExtrude","SWEPT_FACE",FACE,{"disambiguationData":[OSD([sQuery(id+"F6.wireOp",EDGE,"E25.MirrorCS")])]})])],"derivedFrom":makeQuery(id+"F3.opExtrude","CAP_EDGE",EDGE,{"disambiguationData":[OSD([subQ0])],"isStart":false})});}
            var Q72;
            Q72=makeQuery(id+"F7.boolean.opBoolean","INTERSECT",EDGE,{"derivedFrom":[makeQuery(id+"F3.opExtrude","SWEPT_FACE",FACE,{"disambiguationData":[OSD([sQuery(id+"F2.wireOp",EDGE,"E6.left")])]}),makeQuery(id+"F7.opExtrude","SWEPT_FACE",FACE,{"disambiguationData":[OSD([sQuery(id+"F6.wireOp",EDGE,"E41.MirrorCS")])]})]});
            var Q73;
            {var subQ0=sQuery(id+"F2.wireOp",EDGE,"E6.left");Q73=makeQuery(id+"F7.boolean.opBoolean","SPLIT",EDGE,{"disambiguationData":[TD([makeQuery(id+"F7.opExtrude","SWEPT_FACE",FACE,{"disambiguationData":[OSD([sQuery(id+"F6.wireOp",EDGE,"E22.MirrorCS")])]})])],"derivedFrom":makeQuery(id+"F3.opExtrude","CAP_EDGE",EDGE,{"disambiguationData":[OSD([subQ0])],"isStart":false})});}
            var Q74;
            Q74=makeQuery(id+"F7.boolean.opBoolean","INTERSECT",EDGE,{"derivedFrom":[makeQuery(id+"F3.opExtrude","SWEPT_FACE",FACE,{"disambiguationData":[OSD([sQuery(id+"F2.wireOp",EDGE,"E6.left")])]}),makeQuery(id+"F7.opExtrude","SWEPT_FACE",FACE,{"disambiguationData":[OSD([sQuery(id+"F6.wireOp",EDGE,"E33.MirrorCS")])]})]});
            var Q75;
            {var subQ0=sQuery(id+"F2.wireOp",EDGE,"E6.left");Q75=makeQuery(id+"F7.boolean.opBoolean","SPLIT",EDGE,{"disambiguationData":[TD([makeQuery(id+"F7.opExtrude","SWEPT_FACE",FACE,{"disambiguationData":[OSD([sQuery(id+"F6.wireOp",EDGE,"E29.MirrorCS")])]})])],"derivedFrom":makeQuery(id+"F3.opExtrude","CAP_EDGE",EDGE,{"disambiguationData":[OSD([subQ0])],"isStart":false})});}
            var Q76;
            Q76=makeQuery(id+"F7.boolean.opBoolean","INTERSECT",EDGE,{"derivedFrom":[makeQuery(id+"F3.opExtrude","SWEPT_FACE",FACE,{"disambiguationData":[OSD([sQuery(id+"F2.wireOp",EDGE,"E6.left")])]}),makeQuery(id+"F7.opExtrude","SWEPT_FACE",FACE,{"disambiguationData":[OSD([sQuery(id+"F6.wireOp",EDGE,"E37.MirrorCS")])]})]});
            var Q77;
            {var subQ0=sQuery(id+"F2.wireOp",EDGE,"E6.bottom");var subQ1=sQuery(id+"F2.wireOp",EDGE,"E6.left");Q77=makeQuery(id+"F7.boolean.opBoolean","SPLIT",EDGE,{"disambiguationData":[TD([makeQuery(id+"F3.opExtrude","SWEPT_FACE",FACE,{"disambiguationData":[OSD([subQ0])]})])],"derivedFrom":makeQuery(id+"F3.opExtrude","CAP_EDGE",EDGE,{"disambiguationData":[OSD([subQ1])],"isStart":false})});}
            var Q78;
            Q78=makeQuery(id+"F7.boolean.opBoolean","INTERSECT",EDGE,{"derivedFrom":[makeQuery(id+"F3.opExtrude","SWEPT_FACE",FACE,{"disambiguationData":[OSD([sQuery(id+"F2.wireOp",EDGE,"E6.left")])]}),makeQuery(id+"F7.opExtrude","SWEPT_FACE",FACE,{"disambiguationData":[OSD([sQuery(id+"F6.wireOp",EDGE,"E32.MirrorCS")])]})]});
            var Q79;
            {var subQ0=sQuery(id+"F2.wireOp",EDGE,"E5.left");var subQ1=sQuery(id+"F2.wireOp",EDGE,"E5.top");Q79=makeQuery(id+"F7.boolean.opBoolean","SPLIT",EDGE,{"disambiguationData":[TD([makeQuery(id+"F3.opExtrude","SWEPT_FACE",FACE,{"disambiguationData":[OSD([subQ1])]})])],"derivedFrom":makeQuery(id+"F3.opExtrude","CAP_EDGE",EDGE,{"disambiguationData":[OSD([subQ0])],"isStart":false})});}
            var Q80;
            Q80=makeQuery(id+"F7.boolean.opBoolean","INTERSECT",EDGE,{"derivedFrom":[makeQuery(id+"F3.opExtrude","SWEPT_FACE",FACE,{"disambiguationData":[OSD([sQuery(id+"F2.wireOp",EDGE,"E5.left")])]}),makeQuery(id+"F7.opExtrude","SWEPT_FACE",FACE,{"disambiguationData":[OSD([sQuery(id+"F6.wireOp",EDGE,"E32.MirrorCS")])]})]});
            var Q81;
            {var subQ0=sQuery(id+"F2.wireOp",EDGE,"E5.left");Q81=makeQuery(id+"F7.boolean.opBoolean","SPLIT",EDGE,{"disambiguationData":[TD([makeQuery(id+"F7.opExtrude","SWEPT_FACE",FACE,{"disambiguationData":[OSD([sQuery(id+"F6.wireOp",EDGE,"E24.MirrorCS")])]})])],"derivedFrom":makeQuery(id+"F3.opExtrude","CAP_EDGE",EDGE,{"disambiguationData":[OSD([subQ0])],"isStart":false})});}
            var Q82;
            Q82=makeQuery(id+"F7.boolean.opBoolean","INTERSECT",EDGE,{"derivedFrom":[makeQuery(id+"F3.opExtrude","SWEPT_FACE",FACE,{"disambiguationData":[OSD([sQuery(id+"F2.wireOp",EDGE,"E5.left")])]}),makeQuery(id+"F7.opExtrude","SWEPT_FACE",FACE,{"disambiguationData":[OSD([sQuery(id+"F6.wireOp",EDGE,"E40.MirrorCS")])]})]});
            var Q83;
            {var subQ0=sQuery(id+"F2.wireOp",EDGE,"E5.left");Q83=makeQuery(id+"F7.boolean.opBoolean","SPLIT",EDGE,{"disambiguationData":[TD([makeQuery(id+"F7.opExtrude","SWEPT_FACE",FACE,{"disambiguationData":[OSD([sQuery(id+"F6.wireOp",EDGE,"E25.MirrorCS")])]})])],"derivedFrom":makeQuery(id+"F3.opExtrude","CAP_EDGE",EDGE,{"disambiguationData":[OSD([subQ0])],"isStart":false})});}
            var Q84;
            Q84=makeQuery(id+"F7.boolean.opBoolean","INTERSECT",EDGE,{"derivedFrom":[makeQuery(id+"F3.opExtrude","SWEPT_FACE",FACE,{"disambiguationData":[OSD([sQuery(id+"F2.wireOp",EDGE,"E5.left")])]}),makeQuery(id+"F7.opExtrude","SWEPT_FACE",FACE,{"disambiguationData":[OSD([sQuery(id+"F6.wireOp",EDGE,"E41.MirrorCS")])]})]});
            var Q85;
            {var subQ0=sQuery(id+"F2.wireOp",EDGE,"E5.left");Q85=makeQuery(id+"F7.boolean.opBoolean","SPLIT",EDGE,{"disambiguationData":[TD([makeQuery(id+"F7.opExtrude","SWEPT_FACE",FACE,{"disambiguationData":[OSD([sQuery(id+"F6.wireOp",EDGE,"E22.MirrorCS")])]})])],"derivedFrom":makeQuery(id+"F3.opExtrude","CAP_EDGE",EDGE,{"disambiguationData":[OSD([subQ0])],"isStart":false})});}
            var Q86;
            Q86=makeQuery(id+"F7.boolean.opBoolean","INTERSECT",EDGE,{"derivedFrom":[makeQuery(id+"F3.opExtrude","SWEPT_FACE",FACE,{"disambiguationData":[OSD([sQuery(id+"F2.wireOp",EDGE,"E5.left")])]}),makeQuery(id+"F7.opExtrude","SWEPT_FACE",FACE,{"disambiguationData":[OSD([sQuery(id+"F6.wireOp",EDGE,"E33.MirrorCS")])]})]});
            var Q87;
            {var subQ0=sQuery(id+"F2.wireOp",EDGE,"E5.left");Q87=makeQuery(id+"F7.boolean.opBoolean","SPLIT",EDGE,{"disambiguationData":[TD([makeQuery(id+"F7.opExtrude","SWEPT_FACE",FACE,{"disambiguationData":[OSD([sQuery(id+"F6.wireOp",EDGE,"E29.MirrorCS")])]})])],"derivedFrom":makeQuery(id+"F3.opExtrude","CAP_EDGE",EDGE,{"disambiguationData":[OSD([subQ0])],"isStart":false})});}
            var Q88;
            Q88=makeQuery(id+"F7.boolean.opBoolean","INTERSECT",EDGE,{"derivedFrom":[makeQuery(id+"F3.opExtrude","SWEPT_FACE",FACE,{"disambiguationData":[OSD([sQuery(id+"F2.wireOp",EDGE,"E5.left")])]}),makeQuery(id+"F7.opExtrude","SWEPT_FACE",FACE,{"disambiguationData":[OSD([sQuery(id+"F6.wireOp",EDGE,"E37.MirrorCS")])]})]});
            var Q89;
            {var subQ0=sQuery(id+"F2.wireOp",EDGE,"E5.bottom");var subQ1=sQuery(id+"F2.wireOp",EDGE,"E5.left");Q89=makeQuery(id+"F7.boolean.opBoolean","SPLIT",EDGE,{"disambiguationData":[TD([makeQuery(id+"F3.opExtrude","SWEPT_FACE",FACE,{"disambiguationData":[OSD([subQ0])]})])],"derivedFrom":makeQuery(id+"F3.opExtrude","CAP_EDGE",EDGE,{"disambiguationData":[OSD([subQ1])],"isStart":false})});}
            var Q90;
            {var subQ0=sQuery(id+"F2.wireOp",EDGE,"E5.bottom");var subQ1=sQuery(id+"F2.wireOp",EDGE,"E5.right");Q90=makeQuery(id+"F7.boolean.opBoolean","SPLIT",EDGE,{"disambiguationData":[TD([makeQuery(id+"F3.opExtrude","SWEPT_FACE",FACE,{"disambiguationData":[OSD([subQ0])]})])],"derivedFrom":makeQuery(id+"F3.opExtrude","CAP_EDGE",EDGE,{"disambiguationData":[OSD([subQ1])],"isStart":false})});}
            var Q91;
            Q91=makeQuery(id+"F9.boolean.opBoolean","INTERSECT",EDGE,{"derivedFrom":[makeQuery(id+"F7.boolean.opBoolean","COPY",FACE,{"disambiguationData":[TD([makeQuery(id+"F3.opExtrude","SWEPT_FACE",FACE,{"disambiguationData":[OSD([sQuery(id+"F2.wireOp",EDGE,"E5.left")])]})])],"derivedFrom":makeQuery(id+"F7.opExtrude","SWEPT_FACE",FACE,{"disambiguationData":[OSD([sQuery(id+"F6.wireOp",EDGE,"E37.MirrorCS")])]})}),makeQuery(id+"F9.opExtrude","SWEPT_FACE",FACE,{"disambiguationData":[OSD([sQuery(id+"F8.wireOp",EDGE,"E42.left")])]})]});
            var Q92;
            {var subQ0=sQuery(id+"F2.wireOp",EDGE,"E5.right");Q92=makeQuery(id+"F7.boolean.opBoolean","SPLIT",EDGE,{"disambiguationData":[TD([makeQuery(id+"F7.opExtrude","SWEPT_FACE",FACE,{"disambiguationData":[OSD([sQuery(id+"F6.wireOp",EDGE,"E29.MirrorCS")])]})])],"derivedFrom":makeQuery(id+"F3.opExtrude","CAP_EDGE",EDGE,{"disambiguationData":[OSD([subQ0])],"isStart":false})});}
            var Q93;
            Q93=makeQuery(id+"F9.boolean.opBoolean","INTERSECT",EDGE,{"derivedFrom":[makeQuery(id+"F7.boolean.opBoolean","COPY",FACE,{"disambiguationData":[TD([makeQuery(id+"F3.opExtrude","SWEPT_FACE",FACE,{"disambiguationData":[OSD([sQuery(id+"F2.wireOp",EDGE,"E5.left")])]})])],"derivedFrom":makeQuery(id+"F7.opExtrude","SWEPT_FACE",FACE,{"disambiguationData":[OSD([sQuery(id+"F6.wireOp",EDGE,"E33.MirrorCS")])]})}),makeQuery(id+"F9.opExtrude","SWEPT_FACE",FACE,{"disambiguationData":[OSD([sQuery(id+"F8.wireOp",EDGE,"E43.0.1.3")])]})]});
            var Q94;
            {var subQ0=sQuery(id+"F2.wireOp",EDGE,"E5.right");Q94=makeQuery(id+"F7.boolean.opBoolean","SPLIT",EDGE,{"disambiguationData":[TD([makeQuery(id+"F7.opExtrude","SWEPT_FACE",FACE,{"disambiguationData":[OSD([sQuery(id+"F6.wireOp",EDGE,"E22.MirrorCS")])]})])],"derivedFrom":makeQuery(id+"F3.opExtrude","CAP_EDGE",EDGE,{"disambiguationData":[OSD([subQ0])],"isStart":false})});}
            var Q95;
            Q95=makeQuery(id+"F9.boolean.opBoolean","INTERSECT",EDGE,{"derivedFrom":[makeQuery(id+"F7.boolean.opBoolean","COPY",FACE,{"disambiguationData":[TD([makeQuery(id+"F3.opExtrude","SWEPT_FACE",FACE,{"disambiguationData":[OSD([sQuery(id+"F2.wireOp",EDGE,"E5.left")])]})])],"derivedFrom":makeQuery(id+"F7.opExtrude","SWEPT_FACE",FACE,{"disambiguationData":[OSD([sQuery(id+"F6.wireOp",EDGE,"E41.MirrorCS")])]})}),makeQuery(id+"F9.opExtrude","SWEPT_FACE",FACE,{"disambiguationData":[OSD([sQuery(id+"F8.wireOp",EDGE,"E43.0.2.3")])]})]});
            var Q96;
            {var subQ0=sQuery(id+"F2.wireOp",EDGE,"E5.right");Q96=makeQuery(id+"F7.boolean.opBoolean","SPLIT",EDGE,{"disambiguationData":[TD([makeQuery(id+"F7.opExtrude","SWEPT_FACE",FACE,{"disambiguationData":[OSD([sQuery(id+"F6.wireOp",EDGE,"E25.MirrorCS")])]})])],"derivedFrom":makeQuery(id+"F3.opExtrude","CAP_EDGE",EDGE,{"disambiguationData":[OSD([subQ0])],"isStart":false})});}
            var Q97;
            Q97=makeQuery(id+"F9.boolean.opBoolean","INTERSECT",EDGE,{"derivedFrom":[makeQuery(id+"F7.boolean.opBoolean","COPY",FACE,{"disambiguationData":[TD([makeQuery(id+"F3.opExtrude","SWEPT_FACE",FACE,{"disambiguationData":[OSD([sQuery(id+"F2.wireOp",EDGE,"E5.left")])]})])],"derivedFrom":makeQuery(id+"F7.opExtrude","SWEPT_FACE",FACE,{"disambiguationData":[OSD([sQuery(id+"F6.wireOp",EDGE,"E40.MirrorCS")])]})}),makeQuery(id+"F9.opExtrude","SWEPT_FACE",FACE,{"disambiguationData":[OSD([sQuery(id+"F8.wireOp",EDGE,"E43.0.3.3")])]})]});
            var Q98;
            {var subQ0=sQuery(id+"F2.wireOp",EDGE,"E5.right");Q98=makeQuery(id+"F7.boolean.opBoolean","SPLIT",EDGE,{"disambiguationData":[TD([makeQuery(id+"F7.opExtrude","SWEPT_FACE",FACE,{"disambiguationData":[OSD([sQuery(id+"F6.wireOp",EDGE,"E24.MirrorCS")])]})])],"derivedFrom":makeQuery(id+"F3.opExtrude","CAP_EDGE",EDGE,{"disambiguationData":[OSD([subQ0])],"isStart":false})});}
            var Q99;
            Q99=makeQuery(id+"F9.boolean.opBoolean","INTERSECT",EDGE,{"derivedFrom":[makeQuery(id+"F7.boolean.opBoolean","COPY",FACE,{"disambiguationData":[TD([makeQuery(id+"F3.opExtrude","SWEPT_FACE",FACE,{"disambiguationData":[OSD([sQuery(id+"F2.wireOp",EDGE,"E5.left")])]})])],"derivedFrom":makeQuery(id+"F7.opExtrude","SWEPT_FACE",FACE,{"disambiguationData":[OSD([sQuery(id+"F6.wireOp",EDGE,"E32.MirrorCS")])]})}),makeQuery(id+"F9.opExtrude","SWEPT_FACE",FACE,{"disambiguationData":[OSD([sQuery(id+"F8.wireOp",EDGE,"E43.0.4.3")])]})]});
            var Q100;
            {var subQ0=sQuery(id+"F2.wireOp",EDGE,"E5.right");var subQ1=sQuery(id+"F2.wireOp",EDGE,"E5.top");Q100=makeQuery(id+"F7.boolean.opBoolean","SPLIT",EDGE,{"disambiguationData":[TD([makeQuery(id+"F3.opExtrude","SWEPT_FACE",FACE,{"disambiguationData":[OSD([subQ1])]})])],"derivedFrom":makeQuery(id+"F3.opExtrude","CAP_EDGE",EDGE,{"disambiguationData":[OSD([subQ0])],"isStart":false})});}
            var Q101;
            {var subQ0=sQuery(id+"F2.wireOp",EDGE,"E5.bottom");var subQ1=sQuery(id+"F2.wireOp",EDGE,"E5.right");Q101=makeQuery(id+"F7.boolean.opBoolean","SPLIT",EDGE,{"disambiguationData":[TD([makeQuery(id+"F3.opExtrude","SWEPT_FACE",FACE,{"disambiguationData":[OSD([subQ0])]})])],"derivedFrom":makeQuery(id+"F3.opExtrude","CAP_EDGE",EDGE,{"disambiguationData":[OSD([subQ1])],"isStart":true})});}
            var Q102;
            Q102=makeQuery(id+"F9.boolean.opBoolean","INTERSECT",EDGE,{"derivedFrom":[makeQuery(id+"F7.boolean.opBoolean","COPY",FACE,{"disambiguationData":[TD([makeQuery(id+"F3.opExtrude","SWEPT_FACE",FACE,{"disambiguationData":[OSD([sQuery(id+"F2.wireOp",EDGE,"E5.left")])]})])],"derivedFrom":makeQuery(id+"F7.opExtrude","SWEPT_FACE",FACE,{"disambiguationData":[OSD([sQuery(id+"F6.wireOp",EDGE,"E14.4.0.1")])]})}),makeQuery(id+"F9.opExtrude","SWEPT_FACE",FACE,{"disambiguationData":[OSD([sQuery(id+"F8.wireOp",EDGE,"E42.left")])]})]});
            var Q103;
            {var subQ0=sQuery(id+"F2.wireOp",EDGE,"E5.right");Q103=makeQuery(id+"F7.boolean.opBoolean","SPLIT",EDGE,{"disambiguationData":[TD([makeQuery(id+"F7.opExtrude","SWEPT_FACE",FACE,{"disambiguationData":[OSD([sQuery(id+"F6.wireOp",EDGE,"E14.3.0.0")])]})])],"derivedFrom":makeQuery(id+"F3.opExtrude","CAP_EDGE",EDGE,{"disambiguationData":[OSD([subQ0])],"isStart":true})});}
            var Q104;
            Q104=makeQuery(id+"F9.boolean.opBoolean","INTERSECT",EDGE,{"derivedFrom":[makeQuery(id+"F7.boolean.opBoolean","COPY",FACE,{"disambiguationData":[TD([makeQuery(id+"F3.opExtrude","SWEPT_FACE",FACE,{"disambiguationData":[OSD([sQuery(id+"F2.wireOp",EDGE,"E5.left")])]})])],"derivedFrom":makeQuery(id+"F7.opExtrude","SWEPT_FACE",FACE,{"disambiguationData":[OSD([sQuery(id+"F6.wireOp",EDGE,"E14.3.0.1")])]})}),makeQuery(id+"F9.opExtrude","SWEPT_FACE",FACE,{"disambiguationData":[OSD([sQuery(id+"F8.wireOp",EDGE,"E43.0.1.3")])]})]});
            var Q105;
            {var subQ0=sQuery(id+"F2.wireOp",EDGE,"E5.right");Q105=makeQuery(id+"F7.boolean.opBoolean","SPLIT",EDGE,{"disambiguationData":[TD([makeQuery(id+"F7.opExtrude","SWEPT_FACE",FACE,{"disambiguationData":[OSD([sQuery(id+"F6.wireOp",EDGE,"E14.2.0.0")])]})])],"derivedFrom":makeQuery(id+"F3.opExtrude","CAP_EDGE",EDGE,{"disambiguationData":[OSD([subQ0])],"isStart":true})});}
            var Q106;
            Q106=makeQuery(id+"F9.boolean.opBoolean","INTERSECT",EDGE,{"derivedFrom":[makeQuery(id+"F7.boolean.opBoolean","COPY",FACE,{"disambiguationData":[TD([makeQuery(id+"F3.opExtrude","SWEPT_FACE",FACE,{"disambiguationData":[OSD([sQuery(id+"F2.wireOp",EDGE,"E5.left")])]})])],"derivedFrom":makeQuery(id+"F7.opExtrude","SWEPT_FACE",FACE,{"disambiguationData":[OSD([sQuery(id+"F6.wireOp",EDGE,"E14.2.0.1")])]})}),makeQuery(id+"F9.opExtrude","SWEPT_FACE",FACE,{"disambiguationData":[OSD([sQuery(id+"F8.wireOp",EDGE,"E43.0.2.3")])]})]});
            var Q107;
            {var subQ0=sQuery(id+"F2.wireOp",EDGE,"E5.right");Q107=makeQuery(id+"F7.boolean.opBoolean","SPLIT",EDGE,{"disambiguationData":[TD([makeQuery(id+"F7.opExtrude","SWEPT_FACE",FACE,{"disambiguationData":[OSD([sQuery(id+"F6.wireOp",EDGE,"E14.1.0.0")])]})])],"derivedFrom":makeQuery(id+"F3.opExtrude","CAP_EDGE",EDGE,{"disambiguationData":[OSD([subQ0])],"isStart":true})});}
            var Q108;
            Q108=makeQuery(id+"F9.boolean.opBoolean","INTERSECT",EDGE,{"derivedFrom":[makeQuery(id+"F7.boolean.opBoolean","COPY",FACE,{"disambiguationData":[TD([makeQuery(id+"F3.opExtrude","SWEPT_FACE",FACE,{"disambiguationData":[OSD([sQuery(id+"F2.wireOp",EDGE,"E5.left")])]})])],"derivedFrom":makeQuery(id+"F7.opExtrude","SWEPT_FACE",FACE,{"disambiguationData":[OSD([sQuery(id+"F6.wireOp",EDGE,"E14.1.0.1")])]})}),makeQuery(id+"F9.opExtrude","SWEPT_FACE",FACE,{"disambiguationData":[OSD([sQuery(id+"F8.wireOp",EDGE,"E43.0.3.3")])]})]});
            var Q109;
            {var subQ0=sQuery(id+"F2.wireOp",EDGE,"E5.right");Q109=makeQuery(id+"F7.boolean.opBoolean","SPLIT",EDGE,{"disambiguationData":[TD([makeQuery(id+"F7.opExtrude","SWEPT_FACE",FACE,{"disambiguationData":[OSD([sQuery(id+"F6.wireOp",EDGE,"E13")])]})])],"derivedFrom":makeQuery(id+"F3.opExtrude","CAP_EDGE",EDGE,{"disambiguationData":[OSD([subQ0])],"isStart":true})});}
            var Q110;
            Q110=makeQuery(id+"F9.boolean.opBoolean","INTERSECT",EDGE,{"derivedFrom":[makeQuery(id+"F7.boolean.opBoolean","COPY",FACE,{"disambiguationData":[TD([makeQuery(id+"F3.opExtrude","SWEPT_FACE",FACE,{"disambiguationData":[OSD([sQuery(id+"F2.wireOp",EDGE,"E5.left")])]})])],"derivedFrom":makeQuery(id+"F7.opExtrude","SWEPT_FACE",FACE,{"disambiguationData":[OSD([sQuery(id+"F6.wireOp",EDGE,"E12")])]})}),makeQuery(id+"F9.opExtrude","SWEPT_FACE",FACE,{"disambiguationData":[OSD([sQuery(id+"F8.wireOp",EDGE,"E43.0.4.3")])]})]});
            var Q111;
            {var subQ0=sQuery(id+"F2.wireOp",EDGE,"E5.right");var subQ1=sQuery(id+"F2.wireOp",EDGE,"E5.top");Q111=makeQuery(id+"F7.boolean.opBoolean","SPLIT",EDGE,{"disambiguationData":[TD([makeQuery(id+"F3.opExtrude","SWEPT_FACE",FACE,{"disambiguationData":[OSD([subQ1])]})])],"derivedFrom":makeQuery(id+"F3.opExtrude","CAP_EDGE",EDGE,{"disambiguationData":[OSD([subQ0])],"isStart":true})});}
            var Q112;
            {var subQ0=sQuery(id+"F2.wireOp",EDGE,"E6.bottom");var subQ1=sQuery(id+"F2.wireOp",EDGE,"E6.left");Q112=makeQuery(id+"F7.boolean.opBoolean","SPLIT",EDGE,{"disambiguationData":[TD([makeQuery(id+"F3.opExtrude","SWEPT_FACE",FACE,{"disambiguationData":[OSD([subQ0])]})])],"derivedFrom":makeQuery(id+"F3.opExtrude","CAP_EDGE",EDGE,{"disambiguationData":[OSD([subQ1])],"isStart":true})});}
            var Q113;
            {var subQ0=sQuery(id+"F2.wireOp",EDGE,"E6.left");Q113=makeQuery(id+"F7.boolean.opBoolean","SPLIT",EDGE,{"disambiguationData":[TD([makeQuery(id+"F7.opExtrude","SWEPT_FACE",FACE,{"disambiguationData":[OSD([sQuery(id+"F6.wireOp",EDGE,"E14.3.0.0")])]})])],"derivedFrom":makeQuery(id+"F3.opExtrude","CAP_EDGE",EDGE,{"disambiguationData":[OSD([subQ0])],"isStart":true})});}
            var Q114;
            {var subQ0=sQuery(id+"F2.wireOp",EDGE,"E6.left");Q114=makeQuery(id+"F7.boolean.opBoolean","SPLIT",EDGE,{"disambiguationData":[TD([makeQuery(id+"F7.opExtrude","SWEPT_FACE",FACE,{"disambiguationData":[OSD([sQuery(id+"F6.wireOp",EDGE,"E14.2.0.0")])]})])],"derivedFrom":makeQuery(id+"F3.opExtrude","CAP_EDGE",EDGE,{"disambiguationData":[OSD([subQ0])],"isStart":true})});}
            var Q115;
            Q115=makeQuery(id+"F7.boolean.opBoolean","INTERSECT",EDGE,{"derivedFrom":[makeQuery(id+"F3.opExtrude","SWEPT_FACE",FACE,{"disambiguationData":[OSD([sQuery(id+"F2.wireOp",EDGE,"E6.left")])]}),makeQuery(id+"F7.opExtrude","SWEPT_FACE",FACE,{"disambiguationData":[OSD([sQuery(id+"F6.wireOp",EDGE,"E14.3.0.1")])]})]});
            var Q116;
            Q116=makeQuery(id+"F7.boolean.opBoolean","INTERSECT",EDGE,{"derivedFrom":[makeQuery(id+"F3.opExtrude","SWEPT_FACE",FACE,{"disambiguationData":[OSD([sQuery(id+"F2.wireOp",EDGE,"E6.left")])]}),makeQuery(id+"F7.opExtrude","SWEPT_FACE",FACE,{"disambiguationData":[OSD([sQuery(id+"F6.wireOp",EDGE,"E14.4.0.1")])]})]});
            var Q117;
            Q117=makeQuery(id+"F7.boolean.opBoolean","INTERSECT",EDGE,{"derivedFrom":[makeQuery(id+"F3.opExtrude","SWEPT_FACE",FACE,{"disambiguationData":[OSD([sQuery(id+"F2.wireOp",EDGE,"E6.left")])]}),makeQuery(id+"F7.opExtrude","SWEPT_FACE",FACE,{"disambiguationData":[OSD([sQuery(id+"F6.wireOp",EDGE,"E14.2.0.1")])]})]});
            var Q118;
            {var subQ0=sQuery(id+"F2.wireOp",EDGE,"E6.left");Q118=makeQuery(id+"F7.boolean.opBoolean","SPLIT",EDGE,{"disambiguationData":[TD([makeQuery(id+"F7.opExtrude","SWEPT_FACE",FACE,{"disambiguationData":[OSD([sQuery(id+"F6.wireOp",EDGE,"E14.1.0.0")])]})])],"derivedFrom":makeQuery(id+"F3.opExtrude","CAP_EDGE",EDGE,{"disambiguationData":[OSD([subQ0])],"isStart":true})});}
            var Q119;
            Q119=makeQuery(id+"F7.boolean.opBoolean","INTERSECT",EDGE,{"derivedFrom":[makeQuery(id+"F3.opExtrude","SWEPT_FACE",FACE,{"disambiguationData":[OSD([sQuery(id+"F2.wireOp",EDGE,"E6.left")])]}),makeQuery(id+"F7.opExtrude","SWEPT_FACE",FACE,{"disambiguationData":[OSD([sQuery(id+"F6.wireOp",EDGE,"E14.1.0.1")])]})]});
            var Q120;
            {var subQ0=sQuery(id+"F2.wireOp",EDGE,"E6.left");Q120=makeQuery(id+"F7.boolean.opBoolean","SPLIT",EDGE,{"disambiguationData":[TD([makeQuery(id+"F7.opExtrude","SWEPT_FACE",FACE,{"disambiguationData":[OSD([sQuery(id+"F6.wireOp",EDGE,"E13")])]})])],"derivedFrom":makeQuery(id+"F3.opExtrude","CAP_EDGE",EDGE,{"disambiguationData":[OSD([subQ0])],"isStart":true})});}
            var Q121;
            Q121=makeQuery(id+"F7.boolean.opBoolean","INTERSECT",EDGE,{"derivedFrom":[makeQuery(id+"F3.opExtrude","SWEPT_FACE",FACE,{"disambiguationData":[OSD([sQuery(id+"F2.wireOp",EDGE,"E6.left")])]}),makeQuery(id+"F7.opExtrude","SWEPT_FACE",FACE,{"disambiguationData":[OSD([sQuery(id+"F6.wireOp",EDGE,"E12")])]})]});
            var Q122;
            {var subQ0=sQuery(id+"F2.wireOp",EDGE,"E6.left");var subQ1=sQuery(id+"F2.wireOp",EDGE,"E6.top");Q122=makeQuery(id+"F7.boolean.opBoolean","SPLIT",EDGE,{"disambiguationData":[TD([makeQuery(id+"F3.opExtrude","SWEPT_FACE",FACE,{"disambiguationData":[OSD([subQ1])]})])],"derivedFrom":makeQuery(id+"F3.opExtrude","CAP_EDGE",EDGE,{"disambiguationData":[OSD([subQ0])],"isStart":true})});}
            var Q123;
            Q123=makeQuery(id+"F1.opExtrude","SWEPT_EDGE",EDGE,{"disambiguationData":[OSD([sQuery(id+"F0.wireOp",EDGE,"E0.bottom"),sQuery(id+"F0.wireOp",EDGE,"E0.right")])]});
            var Q124;
            {var subQ0=sQuery(id+"F2.wireOp",EDGE,"E5.bottom");var subQ1=sQuery(id+"F2.wireOp",EDGE,"E5.left");Q124=makeQuery(id+"F7.boolean.opBoolean","SPLIT",EDGE,{"disambiguationData":[TD([makeQuery(id+"F3.opExtrude","SWEPT_FACE",FACE,{"disambiguationData":[OSD([subQ0])]})])],"derivedFrom":makeQuery(id+"F3.opExtrude","CAP_EDGE",EDGE,{"disambiguationData":[OSD([subQ1])],"isStart":true})});}
            var Q125;
            {var subQ0=sQuery(id+"F2.wireOp",EDGE,"E5.left");Q125=makeQuery(id+"F7.boolean.opBoolean","SPLIT",EDGE,{"disambiguationData":[TD([makeQuery(id+"F7.opExtrude","SWEPT_FACE",FACE,{"disambiguationData":[OSD([sQuery(id+"F6.wireOp",EDGE,"E14.3.0.0")])]})])],"derivedFrom":makeQuery(id+"F3.opExtrude","CAP_EDGE",EDGE,{"disambiguationData":[OSD([subQ0])],"isStart":true})});}
            var Q126;
            {var subQ0=sQuery(id+"F2.wireOp",EDGE,"E5.left");Q126=makeQuery(id+"F7.boolean.opBoolean","SPLIT",EDGE,{"disambiguationData":[TD([makeQuery(id+"F7.opExtrude","SWEPT_FACE",FACE,{"disambiguationData":[OSD([sQuery(id+"F6.wireOp",EDGE,"E14.2.0.0")])]})])],"derivedFrom":makeQuery(id+"F3.opExtrude","CAP_EDGE",EDGE,{"disambiguationData":[OSD([subQ0])],"isStart":true})});}
            var Q127;
            {var subQ0=sQuery(id+"F2.wireOp",EDGE,"E5.left");Q127=makeQuery(id+"F7.boolean.opBoolean","SPLIT",EDGE,{"disambiguationData":[TD([makeQuery(id+"F7.opExtrude","SWEPT_FACE",FACE,{"disambiguationData":[OSD([sQuery(id+"F6.wireOp",EDGE,"E14.1.0.0")])]})])],"derivedFrom":makeQuery(id+"F3.opExtrude","CAP_EDGE",EDGE,{"disambiguationData":[OSD([subQ0])],"isStart":true})});}
            var Q128;
            {var subQ0=sQuery(id+"F2.wireOp",EDGE,"E5.left");Q128=makeQuery(id+"F7.boolean.opBoolean","SPLIT",EDGE,{"disambiguationData":[TD([makeQuery(id+"F7.opExtrude","SWEPT_FACE",FACE,{"disambiguationData":[OSD([sQuery(id+"F6.wireOp",EDGE,"E13")])]})])],"derivedFrom":makeQuery(id+"F3.opExtrude","CAP_EDGE",EDGE,{"disambiguationData":[OSD([subQ0])],"isStart":true})});}
            var Q129;
            {var subQ0=sQuery(id+"F2.wireOp",EDGE,"E5.left");var subQ1=sQuery(id+"F2.wireOp",EDGE,"E5.top");Q129=makeQuery(id+"F7.boolean.opBoolean","SPLIT",EDGE,{"disambiguationData":[TD([makeQuery(id+"F3.opExtrude","SWEPT_FACE",FACE,{"disambiguationData":[OSD([subQ1])]})])],"derivedFrom":makeQuery(id+"F3.opExtrude","CAP_EDGE",EDGE,{"disambiguationData":[OSD([subQ0])],"isStart":true})});}
            var Q130;
            Q130=makeQuery(id+"F1.opExtrude","SWEPT_EDGE",EDGE,{"disambiguationData":[OSD([sQuery(id+"F0.wireOp",EDGE,"E0.bottom"),sQuery(id+"F0.wireOp",EDGE,"E0.left")])]});
            var Q131;
            Q131=makeQuery(id+"F7.boolean.opBoolean","INTERSECT",EDGE,{"derivedFrom":[makeQuery(id+"F3.opExtrude","SWEPT_FACE",FACE,{"disambiguationData":[OSD([sQuery(id+"F2.wireOp",EDGE,"E5.left")])]}),makeQuery(id+"F7.opExtrude","SWEPT_FACE",FACE,{"disambiguationData":[OSD([sQuery(id+"F6.wireOp",EDGE,"E12")])]})]});
            var Q132;
            Q132=makeQuery(id+"F7.boolean.opBoolean","INTERSECT",EDGE,{"derivedFrom":[makeQuery(id+"F3.opExtrude","SWEPT_FACE",FACE,{"disambiguationData":[OSD([sQuery(id+"F2.wireOp",EDGE,"E5.left")])]}),makeQuery(id+"F7.opExtrude","SWEPT_FACE",FACE,{"disambiguationData":[OSD([sQuery(id+"F6.wireOp",EDGE,"E14.1.0.1")])]})]});
            var Q133;
            Q133=makeQuery(id+"F7.boolean.opBoolean","INTERSECT",EDGE,{"derivedFrom":[makeQuery(id+"F3.opExtrude","SWEPT_FACE",FACE,{"disambiguationData":[OSD([sQuery(id+"F2.wireOp",EDGE,"E5.left")])]}),makeQuery(id+"F7.opExtrude","SWEPT_FACE",FACE,{"disambiguationData":[OSD([sQuery(id+"F6.wireOp",EDGE,"E14.2.0.1")])]})]});
            var Q134;
            Q134=makeQuery(id+"F7.boolean.opBoolean","INTERSECT",EDGE,{"derivedFrom":[makeQuery(id+"F3.opExtrude","SWEPT_FACE",FACE,{"disambiguationData":[OSD([sQuery(id+"F2.wireOp",EDGE,"E5.left")])]}),makeQuery(id+"F7.opExtrude","SWEPT_FACE",FACE,{"disambiguationData":[OSD([sQuery(id+"F6.wireOp",EDGE,"E14.3.0.1")])]})]});
            var Q135;
            Q135=makeQuery(id+"F7.boolean.opBoolean","INTERSECT",EDGE,{"derivedFrom":[makeQuery(id+"F3.opExtrude","SWEPT_FACE",FACE,{"disambiguationData":[OSD([sQuery(id+"F2.wireOp",EDGE,"E5.left")])]}),makeQuery(id+"F7.opExtrude","SWEPT_FACE",FACE,{"disambiguationData":[OSD([sQuery(id+"F6.wireOp",EDGE,"E14.4.0.1")])]})]});
            fillet(context, id + "F13", {"entities" : qUnion([Q0, Q1, Q2, Q3, Q4, Q5, Q6, Q7, Q8, Q9, Q10, Q11, Q12, Q13, Q14, Q15, Q16, Q17, Q18, Q19, Q20, Q21, Q22, Q23, Q24, Q25, Q26, Q27, Q28, Q29, Q30, Q31, Q32, Q33, Q34, Q35, Q36, Q37, Q38, Q39, Q40, Q41, Q42, Q43, Q44, Q45, Q46, Q47, Q48, Q49, Q50, Q51, Q52, Q53, Q54, Q55, Q56, Q57, Q58, Q59, Q60, Q61, Q62, Q63, Q64, Q65, Q66, Q67, Q68, Q69, Q70, Q71, Q72, Q73, Q74, Q75, Q76, Q77, Q78, Q79, Q80, Q81, Q82, Q83, Q84, Q85, Q86, Q87, Q88, Q89, Q90, Q91, Q92, Q93, Q94, Q95, Q96, Q97, Q98, Q99, Q100, Q101, Q102, Q103, Q104, Q105, Q106, Q107, Q108, Q109, Q110, Q111, Q112, Q113, Q114, Q115, Q116, Q117, Q118, Q119, Q120, Q121, Q122, Q123, Q124, Q125, Q126, Q127, Q128, Q129, Q130, Q131, Q132, Q133, Q134, Q135]), "radius" : 2 * mm, "tangentPropagation" : true, "allowEdgeOverflow" : false});
        }
        {
            var Q0;
            Q0=makeQuery(id+"F1.opExtrude","SWEPT_BODY",BODY,{"disambiguationData":[OSD([sQuery(id+"F0.wireOp",EDGE,"E0.bottom"),sQuery(id+"F0.wireOp",EDGE,"E0.top"),sQuery(id+"F0.wireOp",EDGE,"E0.left"),sQuery(id+"F0.wireOp",EDGE,"E0.right")])]});
            var Q1;
            Q1=makeQuery(id+"F1.opExtrude","SWEPT_BODY",BODY,{"disambiguationData":[OSD([sQuery(id+"F0.wireOp",EDGE,"E1.MirrorCS"),sQuery(id+"F0.wireOp",EDGE,"E2.MirrorCS"),sQuery(id+"F0.wireOp",EDGE,"E3.MirrorCS"),sQuery(id+"F0.wireOp",EDGE,"E4.MirrorCS")])]});
            var Q2;
            Q2=makeQuery(id+"F3.opExtrude","SWEPT_BODY",BODY,{"disambiguationData":[OSD([sQuery(id+"F2.wireOp",EDGE,"E6.bottom"),sQuery(id+"F2.wireOp",EDGE,"E6.top"),sQuery(id+"F2.wireOp",EDGE,"E6.left"),sQuery(id+"F2.wireOp",EDGE,"E6.right")])]});
            var Q3;
            Q3=makeQuery(id+"F3.opExtrude","SWEPT_BODY",BODY,{"disambiguationData":[OSD([sQuery(id+"F2.wireOp",EDGE,"E7.bottom"),sQuery(id+"F2.wireOp",EDGE,"E7.top"),sQuery(id+"F2.wireOp",EDGE,"E7.left"),sQuery(id+"F2.wireOp",EDGE,"E7.right")])]});
            var Q4;
            Q4=makeQuery(id+"F12.opExtrude","SWEPT_BODY",BODY,{"disambiguationData":[OSD([sQuery(id+"F11.wireOp",EDGE,"E67.0"),sQuery(id+"F11.wireOp",EDGE,"E67.1"),sQuery(id+"F11.wireOp",EDGE,"E67.2"),sQuery(id+"F11.wireOp",EDGE,"E67.3")])]});
            var Q5;
            Q5=makeQuery(id+"F12.opExtrude","SWEPT_BODY",BODY,{"disambiguationData":[OSD([sQuery(id+"F11.wireOp",EDGE,"E67.4"),sQuery(id+"F11.wireOp",EDGE,"E67.5"),sQuery(id+"F11.wireOp",EDGE,"E67.6"),sQuery(id+"F11.wireOp",EDGE,"E67.7")])]});
            deleteBodies(context, id + "F14", {"entities" : qUnion([Q0, Q1, Q2, Q3, Q4, Q5])});
        }
        {
            var Q0;
            Q0=makeQuery(id+"F3.opExtrude","SWEPT_FACE",FACE,{"disambiguationData":[OSD([sQuery(id+"F2.wireOp",EDGE,"E5.left")])]});
            var sketch = newSketch(context, id + "F15", { "sketchPlane" : qUnion([Q0])});
            skLineSegment(sketch, "E68.bottom", {"start": v(-85, -20) * mm, "end": v(-15, -20) * mm});
            skLineSegment(sketch, "E68.top", {"start": v(-85, -300) * mm, "end": v(-15, -300) * mm});
            skLineSegment(sketch, "E68.left", {"start": v(-85, -20) * mm, "end": v(-85, -300) * mm});
            skLineSegment(sketch, "E68.right", {"start": v(-15, -20) * mm, "end": v(-15, -300) * mm});
            skLineSegment(sketch, "E69", {"start": v(-85, -160) * mm, "end": v(-15, -160) * mm, "construction": true});
            skSolve(sketch);
        }
        {
            var Q0;
            Q0=qSketchRegion(id+"F15",true);
            extrude(context, id + "F16", {"entities" : qUnion([Q0]), "depth" : 30 * mm, "offsetDistance" : 25 * mm});
        }
        {
            var Q0;
            Q0=makeQuery(id+"F3.opExtrude","CAP_EDGE",EDGE,{"disambiguationData":[OSD([sQuery(id+"F2.wireOp",EDGE,"E5.bottom")])],"isStart":true});
            var Q1;
            Q1=makeQuery(id+"F3.opExtrude","CAP_EDGE",EDGE,{"disambiguationData":[OSD([sQuery(id+"F2.wireOp",EDGE,"E5.top")])],"isStart":true});
            fillet(context, id + "F17", {"entities" : qUnion([Q0, Q1]), "radius" : 2 * mm, "tangentPropagation" : true, "allowEdgeOverflow" : false});
        }
    });
